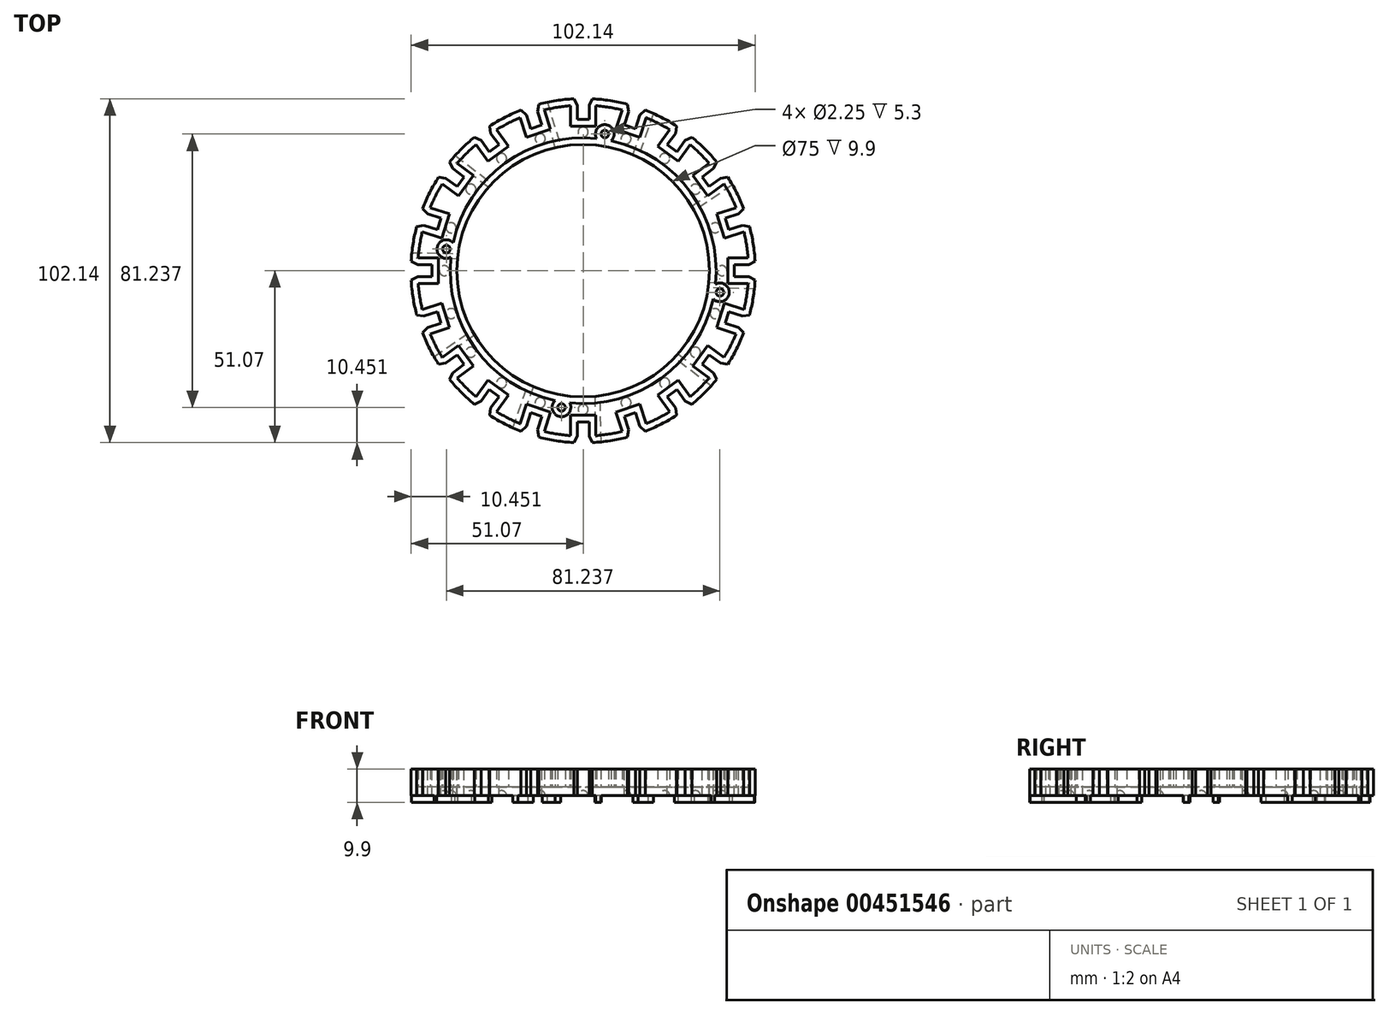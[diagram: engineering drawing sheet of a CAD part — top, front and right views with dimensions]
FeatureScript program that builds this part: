
annotation { "Feature Type Name" : "Feature", "Feature Type Description" : "" }
export const myFeature = defineFeature(function(context is Context, id is Id, definition is map)
    precondition{}
    {
        {
            var Q0;
            Q0=qCreatedBy(makeId("Top.planeOp"),FACE);
            var sketch = newSketch(context, id + "F0", { "sketchPlane" : qUnion([Q0])});
            skLineSegment(sketch, "E0.bottom", {"start": v(-1.78, -44.95) * mm, "end": v(1.77, -44.95) * mm});
            skLineSegment(sketch, "E0.left", {"start": v(-1.78, -44.95) * mm, "end": v(-1.78, -49.15) * mm});
            skLineSegment(sketch, "E0.right", {"start": v(1.77, -44.95) * mm, "end": v(1.77, -49.15) * mm});
            skLineSegment(sketch, "E1.0", {"start": v(-3.78, -42.95) * mm, "end": v(-3.78, -49) * mm});
            skLineSegment(sketch, "E1.1", {"start": v(-3.77, -42.95) * mm, "end": v(3.77, -42.95) * mm});
            skLineSegment(sketch, "E1.2", {"start": v(3.77, -42.95) * mm, "end": v(3.77, -49) * mm});
            skLineSegment(sketch, "E2", {"start": v(1.77, -49.15) * mm, "end": v(2.78, -51.07) * mm});
            skLineSegment(sketch, "E3", {"start": v(-1.78, -49.15) * mm, "end": v(-2.78, -51.07) * mm});
            skPoint(sketch, "E4.center", {"position": v(0, 0) * mm});
            skLineSegment(sketch, "E5.1.0", {"start": v(-16.86, -39.68) * mm, "end": v(-18.73, -45.44) * mm});
            skLineSegment(sketch, "E5.1.1", {"start": v(-9.68, -42.01) * mm, "end": v(-11.55, -47.77) * mm});
            skLineSegment(sketch, "E5.1.2", {"start": v(-16.86, -39.68) * mm, "end": v(-9.68, -42.01) * mm});
            skLineSegment(sketch, "E5.1.3", {"start": v(-12.2, -43.3) * mm, "end": v(-13.5, -47.3) * mm});
            skLineSegment(sketch, "E5.1.4", {"start": v(-16.88, -46.2) * mm, "end": v(-18.42, -47.72) * mm});
            skLineSegment(sketch, "E5.1.5", {"start": v(-15.58, -42.2) * mm, "end": v(-16.88, -46.2) * mm});
            skLineSegment(sketch, "E5.1.6", {"start": v(-13.5, -47.3) * mm, "end": v(-13.14, -49.43) * mm});
            skLineSegment(sketch, "E5.1.7", {"start": v(-15.58, -42.2) * mm, "end": v(-12.2, -43.3) * mm});
            skLineSegment(sketch, "E5.2.0", {"start": v(-28.3, -32.53) * mm, "end": v(-31.86, -37.43) * mm});
            skLineSegment(sketch, "E5.2.1", {"start": v(-22.2, -36.97) * mm, "end": v(-25.75, -41.86) * mm});
            skLineSegment(sketch, "E5.2.2", {"start": v(-28.3, -32.53) * mm, "end": v(-22.2, -36.97) * mm});
            skLineSegment(sketch, "E5.2.3", {"start": v(-24.98, -37.4) * mm, "end": v(-27.45, -40.8) * mm});
            skLineSegment(sketch, "E5.2.4", {"start": v(-30.33, -38.72) * mm, "end": v(-32.27, -39.69) * mm});
            skLineSegment(sketch, "E5.2.5", {"start": v(-27.86, -35.32) * mm, "end": v(-30.33, -38.72) * mm});
            skLineSegment(sketch, "E5.2.6", {"start": v(-27.45, -40.8) * mm, "end": v(-27.78, -42.95) * mm});
            skLineSegment(sketch, "E5.2.7", {"start": v(-27.86, -35.32) * mm, "end": v(-24.98, -37.4) * mm});
            skLineSegment(sketch, "E5.3.0", {"start": v(-36.97, -22.2) * mm, "end": v(-41.86, -25.75) * mm});
            skLineSegment(sketch, "E5.3.1", {"start": v(-32.53, -28.3) * mm, "end": v(-37.43, -31.86) * mm});
            skLineSegment(sketch, "E5.3.2", {"start": v(-36.97, -22.2) * mm, "end": v(-32.53, -28.3) * mm});
            skLineSegment(sketch, "E5.3.3", {"start": v(-35.32, -27.86) * mm, "end": v(-38.72, -30.33) * mm});
            skLineSegment(sketch, "E5.3.4", {"start": v(-40.8, -27.45) * mm, "end": v(-42.95, -27.78) * mm});
            skLineSegment(sketch, "E5.3.5", {"start": v(-37.4, -24.98) * mm, "end": v(-40.8, -27.45) * mm});
            skLineSegment(sketch, "E5.3.6", {"start": v(-38.72, -30.33) * mm, "end": v(-39.69, -32.27) * mm});
            skLineSegment(sketch, "E5.3.7", {"start": v(-37.4, -24.98) * mm, "end": v(-35.32, -27.86) * mm});
            skLineSegment(sketch, "E5.4.0", {"start": v(-42.01, -9.68) * mm, "end": v(-47.77, -11.55) * mm});
            skLineSegment(sketch, "E5.4.1", {"start": v(-39.68, -16.86) * mm, "end": v(-45.44, -18.73) * mm});
            skLineSegment(sketch, "E5.4.2", {"start": v(-42.01, -9.68) * mm, "end": v(-39.68, -16.86) * mm});
            skLineSegment(sketch, "E5.4.3", {"start": v(-42.2, -15.58) * mm, "end": v(-46.2, -16.88) * mm});
            skLineSegment(sketch, "E5.4.4", {"start": v(-47.3, -13.5) * mm, "end": v(-49.43, -13.14) * mm});
            skLineSegment(sketch, "E5.4.5", {"start": v(-43.3, -12.2) * mm, "end": v(-47.3, -13.5) * mm});
            skLineSegment(sketch, "E5.4.6", {"start": v(-46.2, -16.88) * mm, "end": v(-47.72, -18.42) * mm});
            skLineSegment(sketch, "E5.4.7", {"start": v(-43.3, -12.2) * mm, "end": v(-42.2, -15.58) * mm});
            skLineSegment(sketch, "E5.5.0", {"start": v(-42.95, 3.78) * mm, "end": v(-49, 3.78) * mm});
            skLineSegment(sketch, "E5.5.1", {"start": v(-42.95, -3.77) * mm, "end": v(-49, -3.77) * mm});
            skLineSegment(sketch, "E5.5.2", {"start": v(-42.95, 3.78) * mm, "end": v(-42.95, -3.77) * mm});
            skLineSegment(sketch, "E5.5.3", {"start": v(-44.95, -1.77) * mm, "end": v(-49.15, -1.77) * mm});
            skLineSegment(sketch, "E5.5.4", {"start": v(-49.15, 1.78) * mm, "end": v(-51.07, 2.78) * mm});
            skLineSegment(sketch, "E5.5.5", {"start": v(-44.95, 1.78) * mm, "end": v(-49.15, 1.78) * mm});
            skLineSegment(sketch, "E5.5.6", {"start": v(-49.15, -1.77) * mm, "end": v(-51.07, -2.78) * mm});
            skLineSegment(sketch, "E5.5.7", {"start": v(-44.95, 1.78) * mm, "end": v(-44.95, -1.77) * mm});
            skLineSegment(sketch, "E5.6.0", {"start": v(-39.68, 16.86) * mm, "end": v(-45.44, 18.73) * mm});
            skLineSegment(sketch, "E5.6.1", {"start": v(-42.01, 9.68) * mm, "end": v(-47.77, 11.55) * mm});
            skLineSegment(sketch, "E5.6.2", {"start": v(-39.68, 16.86) * mm, "end": v(-42.01, 9.68) * mm});
            skLineSegment(sketch, "E5.6.3", {"start": v(-43.3, 12.2) * mm, "end": v(-47.3, 13.5) * mm});
            skLineSegment(sketch, "E5.6.4", {"start": v(-46.2, 16.88) * mm, "end": v(-47.72, 18.42) * mm});
            skLineSegment(sketch, "E5.6.5", {"start": v(-42.2, 15.58) * mm, "end": v(-46.2, 16.88) * mm});
            skLineSegment(sketch, "E5.6.6", {"start": v(-47.3, 13.5) * mm, "end": v(-49.43, 13.14) * mm});
            skLineSegment(sketch, "E5.6.7", {"start": v(-42.2, 15.58) * mm, "end": v(-43.3, 12.2) * mm});
            skLineSegment(sketch, "E5.7.0", {"start": v(-32.53, 28.3) * mm, "end": v(-37.43, 31.86) * mm});
            skLineSegment(sketch, "E5.7.1", {"start": v(-36.97, 22.2) * mm, "end": v(-41.86, 25.75) * mm});
            skLineSegment(sketch, "E5.7.2", {"start": v(-32.53, 28.3) * mm, "end": v(-36.97, 22.2) * mm});
            skLineSegment(sketch, "E5.7.3", {"start": v(-37.4, 24.98) * mm, "end": v(-40.8, 27.45) * mm});
            skLineSegment(sketch, "E5.7.4", {"start": v(-38.72, 30.33) * mm, "end": v(-39.69, 32.27) * mm});
            skLineSegment(sketch, "E5.7.5", {"start": v(-35.32, 27.86) * mm, "end": v(-38.72, 30.33) * mm});
            skLineSegment(sketch, "E5.7.6", {"start": v(-40.8, 27.45) * mm, "end": v(-42.95, 27.78) * mm});
            skLineSegment(sketch, "E5.7.7", {"start": v(-35.32, 27.86) * mm, "end": v(-37.4, 24.98) * mm});
            skLineSegment(sketch, "E5.8.0", {"start": v(-22.2, 36.97) * mm, "end": v(-25.75, 41.86) * mm});
            skLineSegment(sketch, "E5.8.1", {"start": v(-28.3, 32.53) * mm, "end": v(-31.86, 37.43) * mm});
            skLineSegment(sketch, "E5.8.2", {"start": v(-22.2, 36.97) * mm, "end": v(-28.3, 32.53) * mm});
            skLineSegment(sketch, "E5.8.3", {"start": v(-27.86, 35.32) * mm, "end": v(-30.33, 38.72) * mm});
            skLineSegment(sketch, "E5.8.4", {"start": v(-27.45, 40.8) * mm, "end": v(-27.78, 42.95) * mm});
            skLineSegment(sketch, "E5.8.5", {"start": v(-24.98, 37.4) * mm, "end": v(-27.45, 40.8) * mm});
            skLineSegment(sketch, "E5.8.6", {"start": v(-30.33, 38.72) * mm, "end": v(-32.27, 39.69) * mm});
            skLineSegment(sketch, "E5.8.7", {"start": v(-24.98, 37.4) * mm, "end": v(-27.86, 35.32) * mm});
            skLineSegment(sketch, "E5.9.0", {"start": v(-9.68, 42.01) * mm, "end": v(-11.55, 47.77) * mm});
            skLineSegment(sketch, "E5.9.1", {"start": v(-16.86, 39.68) * mm, "end": v(-18.73, 45.44) * mm});
            skLineSegment(sketch, "E5.9.2", {"start": v(-9.68, 42.01) * mm, "end": v(-16.86, 39.68) * mm});
            skLineSegment(sketch, "E5.9.3", {"start": v(-15.58, 42.2) * mm, "end": v(-16.88, 46.2) * mm});
            skLineSegment(sketch, "E5.9.4", {"start": v(-13.5, 47.3) * mm, "end": v(-13.14, 49.43) * mm});
            skLineSegment(sketch, "E5.9.5", {"start": v(-12.2, 43.3) * mm, "end": v(-13.5, 47.3) * mm});
            skLineSegment(sketch, "E5.9.6", {"start": v(-16.88, 46.2) * mm, "end": v(-18.42, 47.72) * mm});
            skLineSegment(sketch, "E5.9.7", {"start": v(-12.2, 43.3) * mm, "end": v(-15.58, 42.2) * mm});
            skLineSegment(sketch, "E5.10.0", {"start": v(3.78, 42.95) * mm, "end": v(3.78, 49) * mm});
            skLineSegment(sketch, "E5.10.1", {"start": v(-3.77, 42.95) * mm, "end": v(-3.77, 49) * mm});
            skLineSegment(sketch, "E5.10.2", {"start": v(3.78, 42.95) * mm, "end": v(-3.77, 42.95) * mm});
            skLineSegment(sketch, "E5.10.3", {"start": v(-1.77, 44.95) * mm, "end": v(-1.77, 49.15) * mm});
            skLineSegment(sketch, "E5.10.4", {"start": v(1.78, 49.15) * mm, "end": v(2.78, 51.07) * mm});
            skLineSegment(sketch, "E5.10.5", {"start": v(1.78, 44.95) * mm, "end": v(1.78, 49.15) * mm});
            skLineSegment(sketch, "E5.10.6", {"start": v(-1.77, 49.15) * mm, "end": v(-2.78, 51.07) * mm});
            skLineSegment(sketch, "E5.10.7", {"start": v(1.78, 44.95) * mm, "end": v(-1.77, 44.95) * mm});
            skLineSegment(sketch, "E5.11.0", {"start": v(16.86, 39.68) * mm, "end": v(18.73, 45.44) * mm});
            skLineSegment(sketch, "E5.11.1", {"start": v(9.68, 42.01) * mm, "end": v(11.55, 47.77) * mm});
            skLineSegment(sketch, "E5.11.2", {"start": v(16.86, 39.68) * mm, "end": v(9.68, 42.01) * mm});
            skLineSegment(sketch, "E5.11.3", {"start": v(12.2, 43.3) * mm, "end": v(13.5, 47.3) * mm});
            skLineSegment(sketch, "E5.11.4", {"start": v(16.88, 46.2) * mm, "end": v(18.42, 47.72) * mm});
            skLineSegment(sketch, "E5.11.5", {"start": v(15.58, 42.2) * mm, "end": v(16.88, 46.2) * mm});
            skLineSegment(sketch, "E5.11.6", {"start": v(13.5, 47.3) * mm, "end": v(13.14, 49.43) * mm});
            skLineSegment(sketch, "E5.11.7", {"start": v(15.58, 42.2) * mm, "end": v(12.2, 43.3) * mm});
            skLineSegment(sketch, "E5.12.0", {"start": v(28.3, 32.53) * mm, "end": v(31.86, 37.43) * mm});
            skLineSegment(sketch, "E5.12.1", {"start": v(22.2, 36.97) * mm, "end": v(25.75, 41.86) * mm});
            skLineSegment(sketch, "E5.12.2", {"start": v(28.3, 32.53) * mm, "end": v(22.2, 36.97) * mm});
            skLineSegment(sketch, "E5.12.3", {"start": v(24.98, 37.4) * mm, "end": v(27.45, 40.8) * mm});
            skLineSegment(sketch, "E5.12.4", {"start": v(30.33, 38.72) * mm, "end": v(32.27, 39.69) * mm});
            skLineSegment(sketch, "E5.12.5", {"start": v(27.86, 35.32) * mm, "end": v(30.33, 38.72) * mm});
            skLineSegment(sketch, "E5.12.6", {"start": v(27.45, 40.8) * mm, "end": v(27.78, 42.95) * mm});
            skLineSegment(sketch, "E5.12.7", {"start": v(27.86, 35.32) * mm, "end": v(24.98, 37.4) * mm});
            skLineSegment(sketch, "E5.13.0", {"start": v(36.97, 22.2) * mm, "end": v(41.86, 25.75) * mm});
            skLineSegment(sketch, "E5.13.1", {"start": v(32.53, 28.3) * mm, "end": v(37.43, 31.86) * mm});
            skLineSegment(sketch, "E5.13.2", {"start": v(36.97, 22.2) * mm, "end": v(32.53, 28.3) * mm});
            skLineSegment(sketch, "E5.13.3", {"start": v(35.32, 27.86) * mm, "end": v(38.72, 30.33) * mm});
            skLineSegment(sketch, "E5.13.4", {"start": v(40.8, 27.45) * mm, "end": v(42.95, 27.78) * mm});
            skLineSegment(sketch, "E5.13.5", {"start": v(37.4, 24.98) * mm, "end": v(40.8, 27.45) * mm});
            skLineSegment(sketch, "E5.13.6", {"start": v(38.72, 30.33) * mm, "end": v(39.69, 32.27) * mm});
            skLineSegment(sketch, "E5.13.7", {"start": v(37.4, 24.98) * mm, "end": v(35.32, 27.86) * mm});
            skLineSegment(sketch, "E5.14.0", {"start": v(42.01, 9.68) * mm, "end": v(47.77, 11.55) * mm});
            skLineSegment(sketch, "E5.14.1", {"start": v(39.68, 16.86) * mm, "end": v(45.44, 18.73) * mm});
            skLineSegment(sketch, "E5.14.2", {"start": v(42.01, 9.68) * mm, "end": v(39.68, 16.86) * mm});
            skLineSegment(sketch, "E5.14.3", {"start": v(42.2, 15.58) * mm, "end": v(46.2, 16.88) * mm});
            skLineSegment(sketch, "E5.14.4", {"start": v(47.3, 13.5) * mm, "end": v(49.43, 13.14) * mm});
            skLineSegment(sketch, "E5.14.5", {"start": v(43.3, 12.2) * mm, "end": v(47.3, 13.5) * mm});
            skLineSegment(sketch, "E5.14.6", {"start": v(46.2, 16.88) * mm, "end": v(47.72, 18.42) * mm});
            skLineSegment(sketch, "E5.14.7", {"start": v(43.3, 12.2) * mm, "end": v(42.2, 15.58) * mm});
            skLineSegment(sketch, "E5.15.0", {"start": v(42.95, -3.78) * mm, "end": v(49, -3.78) * mm});
            skLineSegment(sketch, "E5.15.1", {"start": v(42.95, 3.77) * mm, "end": v(49, 3.77) * mm});
            skLineSegment(sketch, "E5.15.2", {"start": v(42.95, -3.78) * mm, "end": v(42.95, 3.77) * mm});
            skLineSegment(sketch, "E5.15.3", {"start": v(44.95, 1.77) * mm, "end": v(49.15, 1.77) * mm});
            skLineSegment(sketch, "E5.15.4", {"start": v(49.15, -1.78) * mm, "end": v(51.07, -2.78) * mm});
            skLineSegment(sketch, "E5.15.5", {"start": v(44.95, -1.78) * mm, "end": v(49.15, -1.78) * mm});
            skLineSegment(sketch, "E5.15.6", {"start": v(49.15, 1.77) * mm, "end": v(51.07, 2.78) * mm});
            skLineSegment(sketch, "E5.15.7", {"start": v(44.95, -1.78) * mm, "end": v(44.95, 1.77) * mm});
            skLineSegment(sketch, "E5.16.0", {"start": v(39.68, -16.86) * mm, "end": v(45.44, -18.73) * mm});
            skLineSegment(sketch, "E5.16.1", {"start": v(42.01, -9.68) * mm, "end": v(47.77, -11.55) * mm});
            skLineSegment(sketch, "E5.16.2", {"start": v(39.68, -16.86) * mm, "end": v(42.01, -9.68) * mm});
            skLineSegment(sketch, "E5.16.3", {"start": v(43.3, -12.2) * mm, "end": v(47.3, -13.5) * mm});
            skLineSegment(sketch, "E5.16.4", {"start": v(46.2, -16.88) * mm, "end": v(47.72, -18.42) * mm});
            skLineSegment(sketch, "E5.16.5", {"start": v(42.2, -15.58) * mm, "end": v(46.2, -16.88) * mm});
            skLineSegment(sketch, "E5.16.6", {"start": v(47.3, -13.5) * mm, "end": v(49.43, -13.14) * mm});
            skLineSegment(sketch, "E5.16.7", {"start": v(42.2, -15.58) * mm, "end": v(43.3, -12.2) * mm});
            skLineSegment(sketch, "E5.17.0", {"start": v(32.53, -28.3) * mm, "end": v(37.43, -31.86) * mm});
            skLineSegment(sketch, "E5.17.1", {"start": v(36.97, -22.2) * mm, "end": v(41.86, -25.75) * mm});
            skLineSegment(sketch, "E5.17.2", {"start": v(32.53, -28.3) * mm, "end": v(36.97, -22.2) * mm});
            skLineSegment(sketch, "E5.17.3", {"start": v(37.4, -24.98) * mm, "end": v(40.8, -27.45) * mm});
            skLineSegment(sketch, "E5.17.4", {"start": v(38.72, -30.33) * mm, "end": v(39.69, -32.27) * mm});
            skLineSegment(sketch, "E5.17.5", {"start": v(35.32, -27.86) * mm, "end": v(38.72, -30.33) * mm});
            skLineSegment(sketch, "E5.17.6", {"start": v(40.8, -27.45) * mm, "end": v(42.95, -27.78) * mm});
            skLineSegment(sketch, "E5.17.7", {"start": v(35.32, -27.86) * mm, "end": v(37.4, -24.98) * mm});
            skLineSegment(sketch, "E5.18.0", {"start": v(22.2, -36.97) * mm, "end": v(25.75, -41.86) * mm});
            skLineSegment(sketch, "E5.18.1", {"start": v(28.3, -32.53) * mm, "end": v(31.86, -37.43) * mm});
            skLineSegment(sketch, "E5.18.2", {"start": v(22.2, -36.97) * mm, "end": v(28.3, -32.53) * mm});
            skLineSegment(sketch, "E5.18.3", {"start": v(27.86, -35.32) * mm, "end": v(30.33, -38.72) * mm});
            skLineSegment(sketch, "E5.18.4", {"start": v(27.45, -40.8) * mm, "end": v(27.78, -42.95) * mm});
            skLineSegment(sketch, "E5.18.5", {"start": v(24.98, -37.4) * mm, "end": v(27.45, -40.8) * mm});
            skLineSegment(sketch, "E5.18.6", {"start": v(30.33, -38.72) * mm, "end": v(32.27, -39.69) * mm});
            skLineSegment(sketch, "E5.18.7", {"start": v(24.98, -37.4) * mm, "end": v(27.86, -35.32) * mm});
            skLineSegment(sketch, "E5.19.0", {"start": v(9.68, -42.01) * mm, "end": v(11.55, -47.77) * mm});
            skLineSegment(sketch, "E5.19.1", {"start": v(16.86, -39.68) * mm, "end": v(18.73, -45.44) * mm});
            skLineSegment(sketch, "E5.19.2", {"start": v(9.68, -42.01) * mm, "end": v(16.86, -39.68) * mm});
            skLineSegment(sketch, "E5.19.3", {"start": v(15.58, -42.2) * mm, "end": v(16.88, -46.2) * mm});
            skLineSegment(sketch, "E5.19.4", {"start": v(13.5, -47.3) * mm, "end": v(13.14, -49.43) * mm});
            skLineSegment(sketch, "E5.19.5", {"start": v(12.2, -43.3) * mm, "end": v(13.5, -47.3) * mm});
            skLineSegment(sketch, "E5.19.6", {"start": v(16.88, -46.2) * mm, "end": v(18.42, -47.72) * mm});
            skLineSegment(sketch, "E5.19.7", {"start": v(12.2, -43.3) * mm, "end": v(15.58, -42.2) * mm});
            skLineSegment(sketch, "E5.anchor1", {"start": v(0, 0) * mm, "end": v(-2.78, -51.07) * mm, "construction": true});
            skLineSegment(sketch, "E5.anchor2", {"start": v(0, 0) * mm, "end": v(13.14, -49.43) * mm, "construction": true});
            skArc(sketch, "E6", {"start": v(-3.78, -49) * mm, "mid": v(-7.69, -48.54) * mm, "end": v(-11.55, -47.77) * mm});
            skArc(sketch, "E7", {"start": v(-2.78, -51.07) * mm, "mid": v(-8, -50.52) * mm, "end": v(-13.14, -49.43) * mm});
            skArc(sketch, "E8.1.0", {"start": v(-18.73, -45.44) * mm, "mid": v(-22.31, -43.8) * mm, "end": v(-25.75, -41.86) * mm});
            skArc(sketch, "E8.1.1", {"start": v(-18.42, -47.72) * mm, "mid": v(-23.22, -45.57) * mm, "end": v(-27.78, -42.95) * mm});
            skArc(sketch, "E8.2.0", {"start": v(-31.86, -37.43) * mm, "mid": v(-34.75, -34.75) * mm, "end": v(-37.43, -31.86) * mm});
            skArc(sketch, "E8.2.1", {"start": v(-32.27, -39.69) * mm, "mid": v(-36.17, -36.17) * mm, "end": v(-39.69, -32.27) * mm});
            skArc(sketch, "E8.3.0", {"start": v(-41.86, -25.75) * mm, "mid": v(-43.8, -22.31) * mm, "end": v(-45.44, -18.73) * mm});
            skArc(sketch, "E8.3.1", {"start": v(-42.95, -27.78) * mm, "mid": v(-45.57, -23.22) * mm, "end": v(-47.72, -18.42) * mm});
            skArc(sketch, "E8.4.0", {"start": v(-47.77, -11.55) * mm, "mid": v(-48.54, -7.69) * mm, "end": v(-49, -3.77) * mm});
            skArc(sketch, "E8.4.1", {"start": v(-49.43, -13.14) * mm, "mid": v(-50.52, -8) * mm, "end": v(-51.07, -2.78) * mm});
            skArc(sketch, "E8.5.0", {"start": v(-49, 3.78) * mm, "mid": v(-48.54, 7.69) * mm, "end": v(-47.77, 11.55) * mm});
            skArc(sketch, "E8.5.1", {"start": v(-51.07, 2.78) * mm, "mid": v(-50.52, 8) * mm, "end": v(-49.43, 13.14) * mm});
            skArc(sketch, "E8.6.0", {"start": v(-45.44, 18.73) * mm, "mid": v(-43.8, 22.31) * mm, "end": v(-41.86, 25.75) * mm});
            skArc(sketch, "E8.6.1", {"start": v(-47.72, 18.42) * mm, "mid": v(-45.57, 23.22) * mm, "end": v(-42.95, 27.78) * mm});
            skArc(sketch, "E8.7.0", {"start": v(-37.43, 31.86) * mm, "mid": v(-34.75, 34.75) * mm, "end": v(-31.86, 37.43) * mm});
            skArc(sketch, "E8.7.1", {"start": v(-39.69, 32.27) * mm, "mid": v(-36.17, 36.17) * mm, "end": v(-32.27, 39.69) * mm});
            skArc(sketch, "E8.8.0", {"start": v(-25.75, 41.86) * mm, "mid": v(-22.31, 43.8) * mm, "end": v(-18.73, 45.44) * mm});
            skArc(sketch, "E8.8.1", {"start": v(-27.78, 42.95) * mm, "mid": v(-23.22, 45.57) * mm, "end": v(-18.42, 47.72) * mm});
            skArc(sketch, "E8.9.0", {"start": v(-11.55, 47.77) * mm, "mid": v(-7.69, 48.54) * mm, "end": v(-3.77, 49) * mm});
            skArc(sketch, "E8.9.1", {"start": v(-13.14, 49.43) * mm, "mid": v(-8, 50.52) * mm, "end": v(-2.78, 51.07) * mm});
            skArc(sketch, "E8.10.0", {"start": v(3.78, 49) * mm, "mid": v(7.69, 48.54) * mm, "end": v(11.55, 47.77) * mm});
            skArc(sketch, "E8.10.1", {"start": v(2.78, 51.07) * mm, "mid": v(8, 50.52) * mm, "end": v(13.14, 49.43) * mm});
            skArc(sketch, "E8.11.0", {"start": v(18.73, 45.44) * mm, "mid": v(22.31, 43.8) * mm, "end": v(25.75, 41.86) * mm});
            skArc(sketch, "E8.11.1", {"start": v(18.42, 47.72) * mm, "mid": v(23.22, 45.57) * mm, "end": v(27.78, 42.95) * mm});
            skArc(sketch, "E8.12.0", {"start": v(31.86, 37.43) * mm, "mid": v(34.75, 34.75) * mm, "end": v(37.43, 31.86) * mm});
            skArc(sketch, "E8.12.1", {"start": v(32.27, 39.69) * mm, "mid": v(36.17, 36.17) * mm, "end": v(39.69, 32.27) * mm});
            skArc(sketch, "E8.13.0", {"start": v(41.86, 25.75) * mm, "mid": v(43.8, 22.31) * mm, "end": v(45.44, 18.73) * mm});
            skArc(sketch, "E8.13.1", {"start": v(42.95, 27.78) * mm, "mid": v(45.57, 23.22) * mm, "end": v(47.72, 18.42) * mm});
            skArc(sketch, "E8.14.0", {"start": v(47.77, 11.55) * mm, "mid": v(48.54, 7.69) * mm, "end": v(49, 3.77) * mm});
            skArc(sketch, "E8.14.1", {"start": v(49.43, 13.14) * mm, "mid": v(50.52, 8) * mm, "end": v(51.07, 2.78) * mm});
            skArc(sketch, "E8.15.0", {"start": v(49, -3.78) * mm, "mid": v(48.54, -7.69) * mm, "end": v(47.77, -11.55) * mm});
            skArc(sketch, "E8.15.1", {"start": v(51.07, -2.78) * mm, "mid": v(50.52, -8) * mm, "end": v(49.43, -13.14) * mm});
            skArc(sketch, "E8.16.0", {"start": v(45.44, -18.73) * mm, "mid": v(43.8, -22.31) * mm, "end": v(41.86, -25.75) * mm});
            skArc(sketch, "E8.16.1", {"start": v(47.72, -18.42) * mm, "mid": v(45.57, -23.22) * mm, "end": v(42.95, -27.78) * mm});
            skArc(sketch, "E8.17.0", {"start": v(37.43, -31.86) * mm, "mid": v(34.75, -34.75) * mm, "end": v(31.86, -37.43) * mm});
            skArc(sketch, "E8.17.1", {"start": v(39.69, -32.27) * mm, "mid": v(36.17, -36.17) * mm, "end": v(32.27, -39.69) * mm});
            skArc(sketch, "E8.18.0", {"start": v(25.75, -41.86) * mm, "mid": v(22.31, -43.8) * mm, "end": v(18.73, -45.44) * mm});
            skArc(sketch, "E8.18.1", {"start": v(27.78, -42.95) * mm, "mid": v(23.22, -45.57) * mm, "end": v(18.42, -47.72) * mm});
            skArc(sketch, "E8.19.0", {"start": v(11.55, -47.77) * mm, "mid": v(7.69, -48.54) * mm, "end": v(3.77, -49) * mm});
            skArc(sketch, "E8.19.1", {"start": v(13.14, -49.43) * mm, "mid": v(8, -50.52) * mm, "end": v(2.78, -51.07) * mm});
            skLineSegment(sketch, "E8.anchor1", {"start": v(0, 0) * mm, "end": v(-13.14, -49.43) * mm, "construction": true});
            skLineSegment(sketch, "E8.anchor2", {"start": v(0, 0) * mm, "end": v(2.78, -51.07) * mm, "construction": true});
            skLineSegment(sketch, "E9", {"start": v(0, 0) * mm, "end": v(-7.69, -48.54) * mm, "construction": true});
            skCircle(sketch, "E10", {"center": v(0, 0) * mm, "radius": 37.5 * mm});
            skArc(sketch, "E11.0", {"start": v(39.3, -4) * mm, "mid": v(31.96, 23.22) * mm, "end": v(8.35, 38.6) * mm});
            skCircle(sketch, "E12", {"center": v(-6.43, -40.62) * mm, "radius": 2.77 * mm});
            skCircle(sketch, "E13.0", {"center": v(-6.43, -40.62) * mm, "radius": 1.13 * mm});
            skCircle(sketch, "E14.1.0", {"center": v(-40.62, 6.43) * mm, "radius": 2.77 * mm});
            skCircle(sketch, "E14.1.1", {"center": v(-40.62, 6.43) * mm, "radius": 1.13 * mm});
            skCircle(sketch, "E14.2.0", {"center": v(6.43, 40.62) * mm, "radius": 2.77 * mm});
            skCircle(sketch, "E14.2.1", {"center": v(6.43, 40.62) * mm, "radius": 1.13 * mm});
            skCircle(sketch, "E14.3.0", {"center": v(40.62, -6.43) * mm, "radius": 2.77 * mm});
            skCircle(sketch, "E14.3.1", {"center": v(40.62, -6.43) * mm, "radius": 1.13 * mm});
            skLineSegment(sketch, "E14.anchor1", {"start": v(0, 0) * mm, "end": v(-6.43, -40.62) * mm, "construction": true});
            skLineSegment(sketch, "E14.anchor2", {"start": v(0, 0) * mm, "end": v(40.62, -6.43) * mm, "construction": true});
            skArc(sketch, "E15.trimOffspring", {"start": v(4, 39.3) * mm, "mid": v(-23.22, 31.96) * mm, "end": v(-38.6, 8.35) * mm});
            skArc(sketch, "E16.trimOffspring", {"start": v(-39.3, 4) * mm, "mid": v(-31.96, -23.22) * mm, "end": v(-8.35, -38.6) * mm});
            skArc(sketch, "E17.trimOffspring", {"start": v(-4, -39.3) * mm, "mid": v(23.22, -31.96) * mm, "end": v(38.6, -8.35) * mm});
            skSolve(sketch);
        }
        {
            var Q0;
            Q0=makeQuery(id+"F0.imprint","IMPRINT",FACE,{"disambiguationData":[TD([[makeQuery(id+"F0.imprint","IMPRINT",EDGE,{"derivedFrom":sQuery(id+"F0.wireOp",EDGE,"E1.0")}),-1.0]])]});
            var Q1;
            Q1=makeQuery(id+"F0.imprint","IMPRINT",FACE,{"disambiguationData":[TD([[makeQuery(id+"F0.imprint","IMPRINT",EDGE,{"derivedFrom":sQuery(id+"F0.wireOp",EDGE,"E0.bottom")}),1.0]])]});
            var Q2;
            Q2=makeQuery(id+"F0.imprint","IMPRINT",FACE,{"disambiguationData":[TD([[makeQuery(id+"F0.imprint","IMPRINT",EDGE,{"derivedFrom":sQuery(id+"F0.wireOp",EDGE,"E10")}),-1.0]])]});
            var Q3;
            Q3=makeQuery(id+"F0.imprint","IMPRINT",FACE,{"disambiguationData":[TD([[makeQuery(id+"F0.imprint","IMPRINT",EDGE,{"derivedFrom":sQuery(id+"F0.wireOp",EDGE,"E14.2.1")}),-1.0]])]});
            var Q4;
            Q4=makeQuery(id+"F0.imprint","IMPRINT",FACE,{"disambiguationData":[TD([[makeQuery(id+"F0.imprint","IMPRINT",EDGE,{"derivedFrom":sQuery(id+"F0.wireOp",EDGE,"E14.2.1")}),1.0]])]});
            var Q5;
            Q5=makeQuery(id+"F0.imprint","IMPRINT",FACE,{"disambiguationData":[TD([[makeQuery(id+"F0.imprint","IMPRINT",EDGE,{"derivedFrom":sQuery(id+"F0.wireOp",EDGE,"E14.1.1")}),-1.0]])]});
            var Q6;
            Q6=makeQuery(id+"F0.imprint","IMPRINT",FACE,{"disambiguationData":[TD([[makeQuery(id+"F0.imprint","IMPRINT",EDGE,{"derivedFrom":sQuery(id+"F0.wireOp",EDGE,"E14.1.1")}),1.0]])]});
            var Q7;
            Q7=makeQuery(id+"F0.imprint","IMPRINT",FACE,{"disambiguationData":[TD([[makeQuery(id+"F0.imprint","IMPRINT",EDGE,{"derivedFrom":sQuery(id+"F0.wireOp",EDGE,"E13.0")}),-1.0]])]});
            var Q8;
            Q8=makeQuery(id+"F0.imprint","IMPRINT",FACE,{"disambiguationData":[TD([[makeQuery(id+"F0.imprint","IMPRINT",EDGE,{"derivedFrom":sQuery(id+"F0.wireOp",EDGE,"E13.0")}),1.0]])]});
            var Q9;
            Q9=makeQuery(id+"F0.imprint","IMPRINT",FACE,{"disambiguationData":[TD([[makeQuery(id+"F0.imprint","IMPRINT",EDGE,{"derivedFrom":sQuery(id+"F0.wireOp",EDGE,"E14.3.1")}),-1.0]])]});
            var Q10;
            Q10=makeQuery(id+"F0.imprint","IMPRINT",FACE,{"disambiguationData":[TD([[makeQuery(id+"F0.imprint","IMPRINT",EDGE,{"derivedFrom":sQuery(id+"F0.wireOp",EDGE,"E14.3.1")}),1.0]])]});
            extrude(context, id + "F1", {"entities" : qUnion([Q0, Q1, Q2, Q3, Q4, Q5, Q6, Q7, Q8, Q9, Q10]), "oppositeDirection" : true, "depth" : 2.6 * mm, "offsetDistance" : 25 * mm});
        }
        {
            var Q0;
            Q0=makeQuery(id+"F0.imprint","IMPRINT",FACE,{"disambiguationData":[TD([[makeQuery(id+"F0.imprint","IMPRINT",EDGE,{"derivedFrom":sQuery(id+"F0.wireOp",EDGE,"E0.bottom")}),1.0]])]});
            var Q1;
            Q1=makeQuery(id+"F0.imprint","IMPRINT",FACE,{"disambiguationData":[TD([[makeQuery(id+"F0.imprint","IMPRINT",EDGE,{"derivedFrom":sQuery(id+"F0.wireOp",EDGE,"E10")}),-1.0]])]});
            var Q2;
            Q2=makeQuery(id+"F0.imprint","IMPRINT",FACE,{"disambiguationData":[TD([[makeQuery(id+"F0.imprint","IMPRINT",EDGE,{"derivedFrom":sQuery(id+"F0.wireOp",EDGE,"E14.2.1")}),-1.0]])]});
            var Q3;
            Q3=makeQuery(id+"F0.imprint","IMPRINT",FACE,{"disambiguationData":[TD([[makeQuery(id+"F0.imprint","IMPRINT",EDGE,{"derivedFrom":sQuery(id+"F0.wireOp",EDGE,"E14.3.1")}),-1.0]])]});
            var Q4;
            Q4=makeQuery(id+"F0.imprint","IMPRINT",FACE,{"disambiguationData":[TD([[makeQuery(id+"F0.imprint","IMPRINT",EDGE,{"derivedFrom":sQuery(id+"F0.wireOp",EDGE,"E13.0")}),-1.0]])]});
            var Q5;
            Q5=makeQuery(id+"F0.imprint","IMPRINT",FACE,{"disambiguationData":[TD([[makeQuery(id+"F0.imprint","IMPRINT",EDGE,{"derivedFrom":sQuery(id+"F0.wireOp",EDGE,"E14.1.1")}),-1.0]])]});
            extrude(context, id + "F2", {"entities" : qUnion([Q0, Q1, Q2, Q3, Q4, Q5]), "operationType" : NewBodyOperationType.ADD, "depth" : 5.3 * mm, "offsetDistance" : 25 * mm});
        }
        {
            var Q0;
            Q0=makeQuery(id+"F1.opExtrude","CAP_FACE",FACE,{"disambiguationData":[OSD([sQuery(id+"F0.wireOp",EDGE,"E0.bottom"),sQuery(id+"F0.wireOp",EDGE,"E0.left"),sQuery(id+"F0.wireOp",EDGE,"E0.right"),sQuery(id+"F0.wireOp",EDGE,"E2"),sQuery(id+"F0.wireOp",EDGE,"E3"),sQuery(id+"F0.wireOp",EDGE,"E5.1.3"),sQuery(id+"F0.wireOp",EDGE,"E5.1.4"),sQuery(id+"F0.wireOp",EDGE,"E5.1.5"),sQuery(id+"F0.wireOp",EDGE,"E5.1.6"),sQuery(id+"F0.wireOp",EDGE,"E5.1.7"),sQuery(id+"F0.wireOp",EDGE,"E5.2.3"),sQuery(id+"F0.wireOp",EDGE,"E5.2.4"),sQuery(id+"F0.wireOp",EDGE,"E5.2.5"),sQuery(id+"F0.wireOp",EDGE,"E5.2.6"),sQuery(id+"F0.wireOp",EDGE,"E5.2.7"),sQuery(id+"F0.wireOp",EDGE,"E5.3.3"),sQuery(id+"F0.wireOp",EDGE,"E5.3.4"),sQuery(id+"F0.wireOp",EDGE,"E5.3.5"),sQuery(id+"F0.wireOp",EDGE,"E5.3.6"),sQuery(id+"F0.wireOp",EDGE,"E5.3.7"),sQuery(id+"F0.wireOp",EDGE,"E5.4.3"),sQuery(id+"F0.wireOp",EDGE,"E5.4.4"),sQuery(id+"F0.wireOp",EDGE,"E5.4.5"),sQuery(id+"F0.wireOp",EDGE,"E5.4.6"),sQuery(id+"F0.wireOp",EDGE,"E5.4.7"),sQuery(id+"F0.wireOp",EDGE,"E5.5.3"),sQuery(id+"F0.wireOp",EDGE,"E5.5.4"),sQuery(id+"F0.wireOp",EDGE,"E5.5.5"),sQuery(id+"F0.wireOp",EDGE,"E5.5.6"),sQuery(id+"F0.wireOp",EDGE,"E5.5.7"),sQuery(id+"F0.wireOp",EDGE,"E5.6.3"),sQuery(id+"F0.wireOp",EDGE,"E5.6.4"),sQuery(id+"F0.wireOp",EDGE,"E5.6.5"),sQuery(id+"F0.wireOp",EDGE,"E5.6.6"),sQuery(id+"F0.wireOp",EDGE,"E5.6.7"),sQuery(id+"F0.wireOp",EDGE,"E5.7.3"),sQuery(id+"F0.wireOp",EDGE,"E5.7.4"),sQuery(id+"F0.wireOp",EDGE,"E5.7.5"),sQuery(id+"F0.wireOp",EDGE,"E5.7.6"),sQuery(id+"F0.wireOp",EDGE,"E5.7.7"),sQuery(id+"F0.wireOp",EDGE,"E5.8.3"),sQuery(id+"F0.wireOp",EDGE,"E5.8.4"),sQuery(id+"F0.wireOp",EDGE,"E5.8.5"),sQuery(id+"F0.wireOp",EDGE,"E5.8.6"),sQuery(id+"F0.wireOp",EDGE,"E5.8.7"),sQuery(id+"F0.wireOp",EDGE,"E5.9.3"),sQuery(id+"F0.wireOp",EDGE,"E5.9.4"),sQuery(id+"F0.wireOp",EDGE,"E5.9.5"),sQuery(id+"F0.wireOp",EDGE,"E5.9.6"),sQuery(id+"F0.wireOp",EDGE,"E5.9.7"),sQuery(id+"F0.wireOp",EDGE,"E5.10.3"),sQuery(id+"F0.wireOp",EDGE,"E5.10.4"),sQuery(id+"F0.wireOp",EDGE,"E5.10.5"),sQuery(id+"F0.wireOp",EDGE,"E5.10.6"),sQuery(id+"F0.wireOp",EDGE,"E5.10.7"),sQuery(id+"F0.wireOp",EDGE,"E5.11.3"),sQuery(id+"F0.wireOp",EDGE,"E5.11.4"),sQuery(id+"F0.wireOp",EDGE,"E5.11.5"),sQuery(id+"F0.wireOp",EDGE,"E5.11.6"),sQuery(id+"F0.wireOp",EDGE,"E5.11.7"),sQuery(id+"F0.wireOp",EDGE,"E5.12.3"),sQuery(id+"F0.wireOp",EDGE,"E5.12.4"),sQuery(id+"F0.wireOp",EDGE,"E5.12.5"),sQuery(id+"F0.wireOp",EDGE,"E5.12.6"),sQuery(id+"F0.wireOp",EDGE,"E5.12.7"),sQuery(id+"F0.wireOp",EDGE,"E5.13.3"),sQuery(id+"F0.wireOp",EDGE,"E5.13.4"),sQuery(id+"F0.wireOp",EDGE,"E5.13.5"),sQuery(id+"F0.wireOp",EDGE,"E5.13.6"),sQuery(id+"F0.wireOp",EDGE,"E5.13.7"),sQuery(id+"F0.wireOp",EDGE,"E5.14.3"),sQuery(id+"F0.wireOp",EDGE,"E5.14.4"),sQuery(id+"F0.wireOp",EDGE,"E5.14.5"),sQuery(id+"F0.wireOp",EDGE,"E5.14.6"),sQuery(id+"F0.wireOp",EDGE,"E5.14.7"),sQuery(id+"F0.wireOp",EDGE,"E5.15.3"),sQuery(id+"F0.wireOp",EDGE,"E5.15.4"),sQuery(id+"F0.wireOp",EDGE,"E5.15.5"),sQuery(id+"F0.wireOp",EDGE,"E5.15.6"),sQuery(id+"F0.wireOp",EDGE,"E5.15.7"),sQuery(id+"F0.wireOp",EDGE,"E5.16.3"),sQuery(id+"F0.wireOp",EDGE,"E5.16.4"),sQuery(id+"F0.wireOp",EDGE,"E5.16.5"),sQuery(id+"F0.wireOp",EDGE,"E5.16.6"),sQuery(id+"F0.wireOp",EDGE,"E5.16.7"),sQuery(id+"F0.wireOp",EDGE,"E5.17.3"),sQuery(id+"F0.wireOp",EDGE,"E5.17.4"),sQuery(id+"F0.wireOp",EDGE,"E5.17.5"),sQuery(id+"F0.wireOp",EDGE,"E5.17.6"),sQuery(id+"F0.wireOp",EDGE,"E5.17.7"),sQuery(id+"F0.wireOp",EDGE,"E5.18.3"),sQuery(id+"F0.wireOp",EDGE,"E5.18.4"),sQuery(id+"F0.wireOp",EDGE,"E5.18.5"),sQuery(id+"F0.wireOp",EDGE,"E5.18.6"),sQuery(id+"F0.wireOp",EDGE,"E5.18.7"),sQuery(id+"F0.wireOp",EDGE,"E5.19.3"),sQuery(id+"F0.wireOp",EDGE,"E5.19.4"),sQuery(id+"F0.wireOp",EDGE,"E5.19.5"),sQuery(id+"F0.wireOp",EDGE,"E5.19.6"),sQuery(id+"F0.wireOp",EDGE,"E5.19.7"),sQuery(id+"F0.wireOp",EDGE,"E7"),sQuery(id+"F0.wireOp",EDGE,"E8.1.1"),sQuery(id+"F0.wireOp",EDGE,"E8.2.1"),sQuery(id+"F0.wireOp",EDGE,"E8.3.1"),sQuery(id+"F0.wireOp",EDGE,"E8.4.1"),sQuery(id+"F0.wireOp",EDGE,"E8.5.1"),sQuery(id+"F0.wireOp",EDGE,"E8.6.1"),sQuery(id+"F0.wireOp",EDGE,"E8.7.1"),sQuery(id+"F0.wireOp",EDGE,"E8.8.1"),sQuery(id+"F0.wireOp",EDGE,"E8.9.1"),sQuery(id+"F0.wireOp",EDGE,"E8.10.1"),sQuery(id+"F0.wireOp",EDGE,"E8.11.1"),sQuery(id+"F0.wireOp",EDGE,"E8.12.1"),sQuery(id+"F0.wireOp",EDGE,"E8.13.1"),sQuery(id+"F0.wireOp",EDGE,"E8.14.1"),sQuery(id+"F0.wireOp",EDGE,"E8.15.1"),sQuery(id+"F0.wireOp",EDGE,"E8.16.1"),sQuery(id+"F0.wireOp",EDGE,"E8.17.1"),sQuery(id+"F0.wireOp",EDGE,"E8.18.1"),sQuery(id+"F0.wireOp",EDGE,"E8.19.1"),sQuery(id+"F0.wireOp",EDGE,"E10")])],"isStart":false});
            var sketch = newSketch(context, id + "F3", { "sketchPlane" : qUnion([Q0])});
            skArc(sketch, "E18.0", {"start": v(12.17, 49.68) * mm, "mid": v(11.38, 49.87) * mm, "end": v(10.59, 50.04) * mm});
            skArc(sketch, "E19.0", {"start": v(6.68, 36.9) * mm, "mid": v(7.48, 36.75) * mm, "end": v(8.28, 36.57) * mm});
            skLineSegment(sketch, "E20", {"start": v(10.59, 50.04) * mm, "end": v(6.68, 36.9) * mm});
            skLineSegment(sketch, "E21", {"start": v(8.28, 36.57) * mm, "end": v(12.17, 49.68) * mm});
            skLineSegment(sketch, "E22", {"start": v(5.4, 50.86) * mm, "end": v(5.05, 37.16) * mm});
            skLineSegment(sketch, "E23", {"start": v(3.43, 37.34) * mm, "end": v(3.77, 51.01) * mm});
            skArc(sketch, "E24.trimOffspring", {"start": v(3.43, 37.34) * mm, "mid": v(4.24, 37.26) * mm, "end": v(5.05, 37.16) * mm});
            skArc(sketch, "E25.trimOffspring", {"start": v(5.4, 50.86) * mm, "mid": v(4.58, 50.94) * mm, "end": v(3.77, 51.01) * mm});
            skArc(sketch, "E26.1.0", {"start": v(34.26, 37.98) * mm, "mid": v(33.65, 38.52) * mm, "end": v(33.04, 39.05) * mm});
            skLineSegment(sketch, "E26.1.1", {"start": v(34.26, 37.98) * mm, "end": v(25.93, 27.1) * mm});
            skLineSegment(sketch, "E26.1.2", {"start": v(28.2, 24.72) * mm, "end": v(39.05, 33.04) * mm});
            skArc(sketch, "E26.1.3", {"start": v(24.72, 28.2) * mm, "mid": v(25.33, 27.65) * mm, "end": v(25.93, 27.1) * mm});
            skLineSegment(sketch, "E26.1.4", {"start": v(37.98, 34.26) * mm, "end": v(27.1, 25.93) * mm});
            skLineSegment(sketch, "E26.1.5", {"start": v(24.72, 28.2) * mm, "end": v(33.04, 39.05) * mm});
            skArc(sketch, "E26.1.6", {"start": v(27.1, 25.93) * mm, "mid": v(27.65, 25.33) * mm, "end": v(28.2, 24.72) * mm});
            skArc(sketch, "E26.1.7", {"start": v(39.05, 33.04) * mm, "mid": v(38.52, 33.65) * mm, "end": v(37.98, 34.26) * mm});
            skArc(sketch, "E26.2.0", {"start": v(50.04, 10.59) * mm, "mid": v(49.87, 11.38) * mm, "end": v(49.68, 12.17) * mm});
            skLineSegment(sketch, "E26.2.1", {"start": v(50.04, 10.59) * mm, "end": v(36.9, 6.68) * mm});
            skLineSegment(sketch, "E26.2.2", {"start": v(37.34, 3.43) * mm, "end": v(51.01, 3.77) * mm});
            skArc(sketch, "E26.2.3", {"start": v(36.57, 8.28) * mm, "mid": v(36.75, 7.48) * mm, "end": v(36.9, 6.68) * mm});
            skLineSegment(sketch, "E26.2.4", {"start": v(50.86, 5.4) * mm, "end": v(37.16, 5.05) * mm});
            skLineSegment(sketch, "E26.2.5", {"start": v(36.57, 8.28) * mm, "end": v(49.68, 12.17) * mm});
            skArc(sketch, "E26.2.6", {"start": v(37.16, 5.05) * mm, "mid": v(37.26, 4.24) * mm, "end": v(37.34, 3.43) * mm});
            skArc(sketch, "E26.2.7", {"start": v(51.01, 3.77) * mm, "mid": v(50.94, 4.58) * mm, "end": v(50.86, 5.4) * mm});
            skArc(sketch, "E26.3.0", {"start": v(46.7, -20.85) * mm, "mid": v(47.03, -20.1) * mm, "end": v(47.35, -19.35) * mm});
            skLineSegment(sketch, "E26.3.1", {"start": v(46.7, -20.85) * mm, "end": v(33.78, -16.29) * mm});
            skLineSegment(sketch, "E26.3.2", {"start": v(32.23, -19.18) * mm, "end": v(43.49, -26.93) * mm});
            skArc(sketch, "E26.3.3", {"start": v(34.46, -14.8) * mm, "mid": v(34.13, -15.55) * mm, "end": v(33.78, -16.29) * mm});
            skLineSegment(sketch, "E26.3.4", {"start": v(44.32, -25.53) * mm, "end": v(33.03, -17.76) * mm});
            skLineSegment(sketch, "E26.3.5", {"start": v(34.46, -14.8) * mm, "end": v(47.35, -19.35) * mm});
            skArc(sketch, "E26.3.6", {"start": v(33.03, -17.76) * mm, "mid": v(32.64, -18.47) * mm, "end": v(32.23, -19.18) * mm});
            skArc(sketch, "E26.3.7", {"start": v(43.49, -26.93) * mm, "mid": v(43.9, -26.24) * mm, "end": v(44.32, -25.53) * mm});
            skArc(sketch, "E26.4.0", {"start": v(25.53, -44.32) * mm, "mid": v(26.24, -43.9) * mm, "end": v(26.93, -43.49) * mm});
            skLineSegment(sketch, "E26.4.1", {"start": v(25.53, -44.32) * mm, "end": v(17.76, -33.03) * mm});
            skLineSegment(sketch, "E26.4.2", {"start": v(14.8, -34.46) * mm, "end": v(19.35, -47.35) * mm});
            skArc(sketch, "E26.4.3", {"start": v(19.18, -32.23) * mm, "mid": v(18.47, -32.64) * mm, "end": v(17.76, -33.03) * mm});
            skLineSegment(sketch, "E26.4.4", {"start": v(20.85, -46.7) * mm, "end": v(16.29, -33.78) * mm});
            skLineSegment(sketch, "E26.4.5", {"start": v(19.18, -32.23) * mm, "end": v(26.93, -43.49) * mm});
            skArc(sketch, "E26.4.6", {"start": v(16.29, -33.78) * mm, "mid": v(15.55, -34.13) * mm, "end": v(14.8, -34.46) * mm});
            skArc(sketch, "E26.4.7", {"start": v(19.35, -47.35) * mm, "mid": v(20.1, -47.03) * mm, "end": v(20.85, -46.7) * mm});
            skArc(sketch, "E26.5.0", {"start": v(-5.4, -50.86) * mm, "mid": v(-4.58, -50.94) * mm, "end": v(-3.77, -51.01) * mm});
            skLineSegment(sketch, "E26.5.1", {"start": v(-5.4, -50.86) * mm, "end": v(-5.05, -37.16) * mm});
            skLineSegment(sketch, "E26.5.2", {"start": v(-8.28, -36.57) * mm, "end": v(-12.17, -49.68) * mm});
            skArc(sketch, "E26.5.3", {"start": v(-3.43, -37.34) * mm, "mid": v(-4.24, -37.26) * mm, "end": v(-5.05, -37.16) * mm});
            skLineSegment(sketch, "E26.5.4", {"start": v(-10.59, -50.04) * mm, "end": v(-6.68, -36.9) * mm});
            skLineSegment(sketch, "E26.5.5", {"start": v(-3.43, -37.34) * mm, "end": v(-3.77, -51.01) * mm});
            skArc(sketch, "E26.5.6", {"start": v(-6.68, -36.9) * mm, "mid": v(-7.48, -36.75) * mm, "end": v(-8.28, -36.57) * mm});
            skArc(sketch, "E26.5.7", {"start": v(-12.17, -49.68) * mm, "mid": v(-11.38, -49.87) * mm, "end": v(-10.59, -50.04) * mm});
            skArc(sketch, "E26.6.0", {"start": v(-34.26, -37.98) * mm, "mid": v(-33.65, -38.52) * mm, "end": v(-33.04, -39.05) * mm});
            skLineSegment(sketch, "E26.6.1", {"start": v(-34.26, -37.98) * mm, "end": v(-25.93, -27.1) * mm});
            skLineSegment(sketch, "E26.6.2", {"start": v(-28.2, -24.72) * mm, "end": v(-39.05, -33.04) * mm});
            skArc(sketch, "E26.6.3", {"start": v(-24.72, -28.2) * mm, "mid": v(-25.33, -27.65) * mm, "end": v(-25.93, -27.1) * mm});
            skLineSegment(sketch, "E26.6.4", {"start": v(-37.98, -34.26) * mm, "end": v(-27.1, -25.93) * mm});
            skLineSegment(sketch, "E26.6.5", {"start": v(-24.72, -28.2) * mm, "end": v(-33.04, -39.05) * mm});
            skArc(sketch, "E26.6.6", {"start": v(-27.1, -25.93) * mm, "mid": v(-27.65, -25.33) * mm, "end": v(-28.2, -24.72) * mm});
            skArc(sketch, "E26.6.7", {"start": v(-39.05, -33.04) * mm, "mid": v(-38.52, -33.65) * mm, "end": v(-37.98, -34.26) * mm});
            skArc(sketch, "E26.7.0", {"start": v(-50.04, -10.59) * mm, "mid": v(-49.87, -11.38) * mm, "end": v(-49.68, -12.17) * mm});
            skLineSegment(sketch, "E26.7.1", {"start": v(-50.04, -10.59) * mm, "end": v(-36.9, -6.68) * mm});
            skLineSegment(sketch, "E26.7.2", {"start": v(-37.34, -3.43) * mm, "end": v(-51.01, -3.77) * mm});
            skArc(sketch, "E26.7.3", {"start": v(-36.57, -8.28) * mm, "mid": v(-36.75, -7.48) * mm, "end": v(-36.9, -6.68) * mm});
            skLineSegment(sketch, "E26.7.4", {"start": v(-50.86, -5.4) * mm, "end": v(-37.16, -5.05) * mm});
            skLineSegment(sketch, "E26.7.5", {"start": v(-36.57, -8.28) * mm, "end": v(-49.68, -12.17) * mm});
            skArc(sketch, "E26.7.6", {"start": v(-37.16, -5.05) * mm, "mid": v(-37.26, -4.24) * mm, "end": v(-37.34, -3.43) * mm});
            skArc(sketch, "E26.7.7", {"start": v(-51.01, -3.77) * mm, "mid": v(-50.94, -4.58) * mm, "end": v(-50.86, -5.4) * mm});
            skArc(sketch, "E26.8.0", {"start": v(-46.7, 20.85) * mm, "mid": v(-47.03, 20.1) * mm, "end": v(-47.35, 19.35) * mm});
            skLineSegment(sketch, "E26.8.1", {"start": v(-46.7, 20.85) * mm, "end": v(-33.78, 16.29) * mm});
            skLineSegment(sketch, "E26.8.2", {"start": v(-32.23, 19.18) * mm, "end": v(-43.49, 26.93) * mm});
            skArc(sketch, "E26.8.3", {"start": v(-34.46, 14.8) * mm, "mid": v(-34.13, 15.55) * mm, "end": v(-33.78, 16.29) * mm});
            skLineSegment(sketch, "E26.8.4", {"start": v(-44.32, 25.53) * mm, "end": v(-33.03, 17.76) * mm});
            skLineSegment(sketch, "E26.8.5", {"start": v(-34.46, 14.8) * mm, "end": v(-47.35, 19.35) * mm});
            skArc(sketch, "E26.8.6", {"start": v(-33.03, 17.76) * mm, "mid": v(-32.64, 18.47) * mm, "end": v(-32.23, 19.18) * mm});
            skArc(sketch, "E26.8.7", {"start": v(-43.49, 26.93) * mm, "mid": v(-43.9, 26.24) * mm, "end": v(-44.32, 25.53) * mm});
            skArc(sketch, "E26.9.0", {"start": v(-25.53, 44.32) * mm, "mid": v(-26.24, 43.9) * mm, "end": v(-26.93, 43.49) * mm});
            skLineSegment(sketch, "E26.9.1", {"start": v(-25.53, 44.32) * mm, "end": v(-17.76, 33.03) * mm});
            skLineSegment(sketch, "E26.9.2", {"start": v(-14.8, 34.46) * mm, "end": v(-19.35, 47.35) * mm});
            skArc(sketch, "E26.9.3", {"start": v(-19.18, 32.23) * mm, "mid": v(-18.47, 32.64) * mm, "end": v(-17.76, 33.03) * mm});
            skLineSegment(sketch, "E26.9.4", {"start": v(-20.85, 46.7) * mm, "end": v(-16.29, 33.78) * mm});
            skLineSegment(sketch, "E26.9.5", {"start": v(-19.18, 32.23) * mm, "end": v(-26.93, 43.49) * mm});
            skArc(sketch, "E26.9.6", {"start": v(-16.29, 33.78) * mm, "mid": v(-15.55, 34.13) * mm, "end": v(-14.8, 34.46) * mm});
            skArc(sketch, "E26.9.7", {"start": v(-19.35, 47.35) * mm, "mid": v(-20.1, 47.03) * mm, "end": v(-20.85, 46.7) * mm});
            skLineSegment(sketch, "E26.anchor1", {"start": v(0, 0) * mm, "end": v(3.43, 37.34) * mm, "construction": true});
            skLineSegment(sketch, "E26.anchor2", {"start": v(0, 0) * mm, "end": v(-19.18, 32.23) * mm, "construction": true});
            skSolve(sketch);
        }
        {
            var Q0;
            Q0=makeQuery(id+"F3.imprint","IMPRINT",FACE,{"disambiguationData":[TD([[makeQuery(id+"F3.imprint","IMPRINT",EDGE,{"derivedFrom":sQuery(id+"F3.wireOp",EDGE,"E26.8.0")}),1.0]])]});
            var Q1;
            Q1=makeQuery(id+"F3.imprint","IMPRINT",FACE,{"disambiguationData":[TD([[makeQuery(id+"F3.imprint","IMPRINT",EDGE,{"derivedFrom":sQuery(id+"F3.wireOp",EDGE,"E26.8.2")}),1.0]])]});
            var Q2;
            Q2=makeQuery(id+"F3.imprint","IMPRINT",FACE,{"disambiguationData":[TD([[makeQuery(id+"F3.imprint","IMPRINT",EDGE,{"derivedFrom":sQuery(id+"F3.wireOp",EDGE,"E26.9.0")}),1.0]])]});
            var Q3;
            Q3=makeQuery(id+"F3.imprint","IMPRINT",FACE,{"disambiguationData":[TD([[makeQuery(id+"F3.imprint","IMPRINT",EDGE,{"derivedFrom":sQuery(id+"F3.wireOp",EDGE,"E26.9.2")}),1.0]])]});
            var Q4;
            Q4=makeQuery(id+"F3.imprint","IMPRINT",FACE,{"disambiguationData":[TD([[makeQuery(id+"F3.imprint","IMPRINT",EDGE,{"derivedFrom":sQuery(id+"F3.wireOp",EDGE,"E22")}),-1.0]])]});
            var Q5;
            Q5=makeQuery(id+"F3.imprint","IMPRINT",FACE,{"disambiguationData":[TD([[makeQuery(id+"F3.imprint","IMPRINT",EDGE,{"derivedFrom":sQuery(id+"F3.wireOp",EDGE,"E18.0")}),1.0]])]});
            var Q6;
            Q6=makeQuery(id+"F3.imprint","IMPRINT",FACE,{"disambiguationData":[TD([[makeQuery(id+"F3.imprint","IMPRINT",EDGE,{"derivedFrom":sQuery(id+"F3.wireOp",EDGE,"E26.1.0")}),1.0]])]});
            var Q7;
            Q7=makeQuery(id+"F3.imprint","IMPRINT",FACE,{"disambiguationData":[TD([[makeQuery(id+"F3.imprint","IMPRINT",EDGE,{"derivedFrom":sQuery(id+"F3.wireOp",EDGE,"E26.1.2")}),1.0]])]});
            var Q8;
            Q8=makeQuery(id+"F3.imprint","IMPRINT",FACE,{"disambiguationData":[TD([[makeQuery(id+"F3.imprint","IMPRINT",EDGE,{"derivedFrom":sQuery(id+"F3.wireOp",EDGE,"E26.2.0")}),1.0]])]});
            var Q9;
            Q9=makeQuery(id+"F3.imprint","IMPRINT",FACE,{"disambiguationData":[TD([[makeQuery(id+"F3.imprint","IMPRINT",EDGE,{"derivedFrom":sQuery(id+"F3.wireOp",EDGE,"E26.2.2")}),1.0]])]});
            var Q10;
            Q10=makeQuery(id+"F3.imprint","IMPRINT",FACE,{"disambiguationData":[TD([[makeQuery(id+"F3.imprint","IMPRINT",EDGE,{"derivedFrom":sQuery(id+"F3.wireOp",EDGE,"E26.3.0")}),1.0]])]});
            var Q11;
            Q11=makeQuery(id+"F3.imprint","IMPRINT",FACE,{"disambiguationData":[TD([[makeQuery(id+"F3.imprint","IMPRINT",EDGE,{"derivedFrom":sQuery(id+"F3.wireOp",EDGE,"E26.3.2")}),1.0]])]});
            var Q12;
            Q12=makeQuery(id+"F3.imprint","IMPRINT",FACE,{"disambiguationData":[TD([[makeQuery(id+"F3.imprint","IMPRINT",EDGE,{"derivedFrom":sQuery(id+"F3.wireOp",EDGE,"E26.4.0")}),1.0]])]});
            var Q13;
            Q13=makeQuery(id+"F3.imprint","IMPRINT",FACE,{"disambiguationData":[TD([[makeQuery(id+"F3.imprint","IMPRINT",EDGE,{"derivedFrom":sQuery(id+"F3.wireOp",EDGE,"E26.4.2")}),1.0]])]});
            var Q14;
            Q14=makeQuery(id+"F3.imprint","IMPRINT",FACE,{"disambiguationData":[TD([[makeQuery(id+"F3.imprint","IMPRINT",EDGE,{"derivedFrom":sQuery(id+"F3.wireOp",EDGE,"E26.5.0")}),1.0]])]});
            var Q15;
            Q15=makeQuery(id+"F3.imprint","IMPRINT",FACE,{"disambiguationData":[TD([[makeQuery(id+"F3.imprint","IMPRINT",EDGE,{"derivedFrom":sQuery(id+"F3.wireOp",EDGE,"E26.5.2")}),1.0]])]});
            var Q16;
            Q16=makeQuery(id+"F3.imprint","IMPRINT",FACE,{"disambiguationData":[TD([[makeQuery(id+"F3.imprint","IMPRINT",EDGE,{"derivedFrom":sQuery(id+"F3.wireOp",EDGE,"E26.6.0")}),1.0]])]});
            var Q17;
            Q17=makeQuery(id+"F3.imprint","IMPRINT",FACE,{"disambiguationData":[TD([[makeQuery(id+"F3.imprint","IMPRINT",EDGE,{"derivedFrom":sQuery(id+"F3.wireOp",EDGE,"E26.6.2")}),1.0]])]});
            var Q18;
            Q18=makeQuery(id+"F3.imprint","IMPRINT",FACE,{"disambiguationData":[TD([[makeQuery(id+"F3.imprint","IMPRINT",EDGE,{"derivedFrom":sQuery(id+"F3.wireOp",EDGE,"E26.7.0")}),1.0]])]});
            var Q19;
            Q19=makeQuery(id+"F3.imprint","IMPRINT",FACE,{"disambiguationData":[TD([[makeQuery(id+"F3.imprint","IMPRINT",EDGE,{"derivedFrom":sQuery(id+"F3.wireOp",EDGE,"E26.7.2")}),1.0]])]});
            extrude(context, id + "F4", {"entities" : qUnion([Q0, Q1, Q2, Q3, Q4, Q5, Q6, Q7, Q8, Q9, Q10, Q11, Q12, Q13, Q14, Q15, Q16, Q17, Q18, Q19]), "operationType" : NewBodyOperationType.ADD, "depth" : 2 * mm, "offsetDistance" : 25 * mm});
        }
        {
            var Q0;
            {var subQ0=sQuery(id+"F0.wireOp",EDGE,"E10");var subQ1=sQuery(id+"F0.wireOp",EDGE,"E8.5.1");var subQ2=sQuery(id+"F0.wireOp",EDGE,"E8.4.1");var subQ3=sQuery(id+"F0.wireOp",EDGE,"E5.5.4");var subQ4=sQuery(id+"F0.wireOp",EDGE,"E8.3.1");var subQ5=sQuery(id+"F0.wireOp",EDGE,"E5.5.3");var subQ6=sQuery(id+"F0.wireOp",EDGE,"E5.5.7");var subQ7=sQuery(id+"F0.wireOp",EDGE,"E5.5.6");var subQ8=sQuery(id+"F0.wireOp",EDGE,"E5.5.5");var subQ9=sQuery(id+"F0.wireOp",EDGE,"E5.4.5");var subQ10=sQuery(id+"F0.wireOp",EDGE,"E5.4.6");var subQ11=sQuery(id+"F0.wireOp",EDGE,"E5.4.7");var subQ12=sQuery(id+"F0.wireOp",EDGE,"E5.4.3");var subQ13=sQuery(id+"F0.wireOp",EDGE,"E5.4.4");Q0=makeQuery(id+"F4.boolean.opBoolean","SPLIT",FACE,{"disambiguationData":[TD([makeQuery(id+"F1.opExtrude","SWEPT_FACE",FACE,{"disambiguationData":[OSD([subQ12])]})])],"derivedFrom":makeQuery(id+"F1.opExtrude","CAP_FACE",FACE,{"disambiguationData":[OSD([sQuery(id+"F0.wireOp",EDGE,"E0.bottom"),sQuery(id+"F0.wireOp",EDGE,"E0.left"),sQuery(id+"F0.wireOp",EDGE,"E0.right"),sQuery(id+"F0.wireOp",EDGE,"E2"),sQuery(id+"F0.wireOp",EDGE,"E3"),sQuery(id+"F0.wireOp",EDGE,"E5.1.3"),sQuery(id+"F0.wireOp",EDGE,"E5.1.4"),sQuery(id+"F0.wireOp",EDGE,"E5.1.5"),sQuery(id+"F0.wireOp",EDGE,"E5.1.6"),sQuery(id+"F0.wireOp",EDGE,"E5.1.7"),sQuery(id+"F0.wireOp",EDGE,"E5.2.3"),sQuery(id+"F0.wireOp",EDGE,"E5.2.4"),sQuery(id+"F0.wireOp",EDGE,"E5.2.5"),sQuery(id+"F0.wireOp",EDGE,"E5.2.6"),sQuery(id+"F0.wireOp",EDGE,"E5.2.7"),sQuery(id+"F0.wireOp",EDGE,"E5.3.3"),sQuery(id+"F0.wireOp",EDGE,"E5.3.4"),sQuery(id+"F0.wireOp",EDGE,"E5.3.5"),sQuery(id+"F0.wireOp",EDGE,"E5.3.6"),sQuery(id+"F0.wireOp",EDGE,"E5.3.7"),subQ12,subQ13,subQ9,subQ10,subQ11,subQ5,subQ3,subQ8,subQ7,subQ6,sQuery(id+"F0.wireOp",EDGE,"E5.6.3"),sQuery(id+"F0.wireOp",EDGE,"E5.6.4"),sQuery(id+"F0.wireOp",EDGE,"E5.6.5"),sQuery(id+"F0.wireOp",EDGE,"E5.6.6"),sQuery(id+"F0.wireOp",EDGE,"E5.6.7"),sQuery(id+"F0.wireOp",EDGE,"E5.7.3"),sQuery(id+"F0.wireOp",EDGE,"E5.7.4"),sQuery(id+"F0.wireOp",EDGE,"E5.7.5"),sQuery(id+"F0.wireOp",EDGE,"E5.7.6"),sQuery(id+"F0.wireOp",EDGE,"E5.7.7"),sQuery(id+"F0.wireOp",EDGE,"E5.8.3"),sQuery(id+"F0.wireOp",EDGE,"E5.8.4"),sQuery(id+"F0.wireOp",EDGE,"E5.8.5"),sQuery(id+"F0.wireOp",EDGE,"E5.8.6"),sQuery(id+"F0.wireOp",EDGE,"E5.8.7"),sQuery(id+"F0.wireOp",EDGE,"E5.9.3"),sQuery(id+"F0.wireOp",EDGE,"E5.9.4"),sQuery(id+"F0.wireOp",EDGE,"E5.9.5"),sQuery(id+"F0.wireOp",EDGE,"E5.9.6"),sQuery(id+"F0.wireOp",EDGE,"E5.9.7"),sQuery(id+"F0.wireOp",EDGE,"E5.10.3"),sQuery(id+"F0.wireOp",EDGE,"E5.10.4"),sQuery(id+"F0.wireOp",EDGE,"E5.10.5"),sQuery(id+"F0.wireOp",EDGE,"E5.10.6"),sQuery(id+"F0.wireOp",EDGE,"E5.10.7"),sQuery(id+"F0.wireOp",EDGE,"E5.11.3"),sQuery(id+"F0.wireOp",EDGE,"E5.11.4"),sQuery(id+"F0.wireOp",EDGE,"E5.11.5"),sQuery(id+"F0.wireOp",EDGE,"E5.11.6"),sQuery(id+"F0.wireOp",EDGE,"E5.11.7"),sQuery(id+"F0.wireOp",EDGE,"E5.12.3"),sQuery(id+"F0.wireOp",EDGE,"E5.12.4"),sQuery(id+"F0.wireOp",EDGE,"E5.12.5"),sQuery(id+"F0.wireOp",EDGE,"E5.12.6"),sQuery(id+"F0.wireOp",EDGE,"E5.12.7"),sQuery(id+"F0.wireOp",EDGE,"E5.13.3"),sQuery(id+"F0.wireOp",EDGE,"E5.13.4"),sQuery(id+"F0.wireOp",EDGE,"E5.13.5"),sQuery(id+"F0.wireOp",EDGE,"E5.13.6"),sQuery(id+"F0.wireOp",EDGE,"E5.13.7"),sQuery(id+"F0.wireOp",EDGE,"E5.14.3"),sQuery(id+"F0.wireOp",EDGE,"E5.14.4"),sQuery(id+"F0.wireOp",EDGE,"E5.14.5"),sQuery(id+"F0.wireOp",EDGE,"E5.14.6"),sQuery(id+"F0.wireOp",EDGE,"E5.14.7"),sQuery(id+"F0.wireOp",EDGE,"E5.15.3"),sQuery(id+"F0.wireOp",EDGE,"E5.15.4"),sQuery(id+"F0.wireOp",EDGE,"E5.15.5"),sQuery(id+"F0.wireOp",EDGE,"E5.15.6"),sQuery(id+"F0.wireOp",EDGE,"E5.15.7"),sQuery(id+"F0.wireOp",EDGE,"E5.16.3"),sQuery(id+"F0.wireOp",EDGE,"E5.16.4"),sQuery(id+"F0.wireOp",EDGE,"E5.16.5"),sQuery(id+"F0.wireOp",EDGE,"E5.16.6"),sQuery(id+"F0.wireOp",EDGE,"E5.16.7"),sQuery(id+"F0.wireOp",EDGE,"E5.17.3"),sQuery(id+"F0.wireOp",EDGE,"E5.17.4"),sQuery(id+"F0.wireOp",EDGE,"E5.17.5"),sQuery(id+"F0.wireOp",EDGE,"E5.17.6"),sQuery(id+"F0.wireOp",EDGE,"E5.17.7"),sQuery(id+"F0.wireOp",EDGE,"E5.18.3"),sQuery(id+"F0.wireOp",EDGE,"E5.18.4"),sQuery(id+"F0.wireOp",EDGE,"E5.18.5"),sQuery(id+"F0.wireOp",EDGE,"E5.18.6"),sQuery(id+"F0.wireOp",EDGE,"E5.18.7"),sQuery(id+"F0.wireOp",EDGE,"E5.19.3"),sQuery(id+"F0.wireOp",EDGE,"E5.19.4"),sQuery(id+"F0.wireOp",EDGE,"E5.19.5"),sQuery(id+"F0.wireOp",EDGE,"E5.19.6"),sQuery(id+"F0.wireOp",EDGE,"E5.19.7"),sQuery(id+"F0.wireOp",EDGE,"E7"),sQuery(id+"F0.wireOp",EDGE,"E8.1.1"),sQuery(id+"F0.wireOp",EDGE,"E8.2.1"),subQ4,subQ2,subQ1,sQuery(id+"F0.wireOp",EDGE,"E8.6.1"),sQuery(id+"F0.wireOp",EDGE,"E8.7.1"),sQuery(id+"F0.wireOp",EDGE,"E8.8.1"),sQuery(id+"F0.wireOp",EDGE,"E8.9.1"),sQuery(id+"F0.wireOp",EDGE,"E8.10.1"),sQuery(id+"F0.wireOp",EDGE,"E8.11.1"),sQuery(id+"F0.wireOp",EDGE,"E8.12.1"),sQuery(id+"F0.wireOp",EDGE,"E8.13.1"),sQuery(id+"F0.wireOp",EDGE,"E8.14.1"),sQuery(id+"F0.wireOp",EDGE,"E8.15.1"),sQuery(id+"F0.wireOp",EDGE,"E8.16.1"),sQuery(id+"F0.wireOp",EDGE,"E8.17.1"),sQuery(id+"F0.wireOp",EDGE,"E8.18.1"),sQuery(id+"F0.wireOp",EDGE,"E8.19.1"),subQ0])],"isStart":false})});}
            var sketch = newSketch(context, id + "F5", { "sketchPlane" : qUnion([Q0])});
            skArc(sketch, "E27.0.0", {"start": v(-37.34, -3.43) * mm, "mid": v(-37.04, 5.87) * mm, "end": v(-34.46, 14.8) * mm, "construction": true});
            skLineSegment(sketch, "E27.0.1", {"start": v(-34.46, 14.8) * mm, "end": v(-47.35, 19.35) * mm, "construction": true});
            skArc(sketch, "E27.0.2", {"start": v(-47.35, 19.35) * mm, "mid": v(-47.54, 18.89) * mm, "end": v(-47.72, 18.42) * mm, "construction": true});
            skLineSegment(sketch, "E27.0.3", {"start": v(-47.72, 18.42) * mm, "end": v(-46.2, 16.88) * mm, "construction": true});
            skLineSegment(sketch, "E27.0.4", {"start": v(-46.2, 16.88) * mm, "end": v(-42.2, 15.58) * mm, "construction": true});
            skLineSegment(sketch, "E27.0.5", {"start": v(-42.2, 15.58) * mm, "end": v(-43.3, 12.2) * mm, "construction": true});
            skLineSegment(sketch, "E27.0.6", {"start": v(-43.3, 12.2) * mm, "end": v(-47.3, 13.5) * mm, "construction": true});
            skLineSegment(sketch, "E27.0.7", {"start": v(-47.3, 13.5) * mm, "end": v(-49.43, 13.14) * mm, "construction": true});
            skArc(sketch, "E27.0.8", {"start": v(-49.43, 13.14) * mm, "mid": v(-50.52, 8) * mm, "end": v(-51.07, 2.77) * mm, "construction": true});
            skLineSegment(sketch, "E27.0.9", {"start": v(-51.07, 2.78) * mm, "end": v(-49.15, 1.77) * mm, "construction": true});
            skLineSegment(sketch, "E27.0.10", {"start": v(-49.15, 1.77) * mm, "end": v(-44.95, 1.77) * mm, "construction": true});
            skLineSegment(sketch, "E27.0.11", {"start": v(-44.95, 1.77) * mm, "end": v(-44.95, -1.78) * mm, "construction": true});
            skLineSegment(sketch, "E27.0.12", {"start": v(-44.95, -1.78) * mm, "end": v(-49.15, -1.78) * mm, "construction": true});
            skLineSegment(sketch, "E27.0.13", {"start": v(-49.15, -1.78) * mm, "end": v(-51.07, -2.78) * mm, "construction": true});
            skArc(sketch, "E27.0.14", {"start": v(-51.07, -2.78) * mm, "mid": v(-51.05, -3.27) * mm, "end": v(-51.01, -3.77) * mm, "construction": true});
            skLineSegment(sketch, "E27.0.15", {"start": v(-51.01, -3.77) * mm, "end": v(-37.34, -3.43) * mm, "construction": true});
            skLineSegment(sketch, "E28", {"start": v(-37.78, 12.28) * mm, "end": v(-40.63, 13.2) * mm});
            skLineSegment(sketch, "E29", {"start": v(-39.72, 0) * mm, "end": v(-42.72, 0) * mm});
            skArc(sketch, "E30", {"start": v(-37.78, 12.28) * mm, "mid": v(-38.74, 14.17) * mm, "end": v(-40.63, 13.2) * mm});
            skArc(sketch, "E31", {"start": v(-39.72, 0) * mm, "mid": v(-41.22, 1.5) * mm, "end": v(-42.72, 0) * mm});
            skPoint(sketch, "E32.orphan", {"position": v(-42.75, 13.9) * mm});
            skPoint(sketch, "E33.orphan", {"position": v(-35.66, 11.59) * mm});
            skPoint(sketch, "E34.orphan", {"position": v(-37.5, 0) * mm});
            skPoint(sketch, "E35.orphan", {"position": v(-44.95, 0) * mm});
            skSolve(sketch);
        }
        {
            var Q0;
            Q0=makeQuery(id+"F5.imprint","IMPRINT",FACE,{"disambiguationData":[TD([[makeQuery(id+"F5.imprint","IMPRINT",EDGE,{"derivedFrom":sQuery(id+"F5.wireOp",EDGE,"E28")}),-1.0]])]});
            var Q1;
            Q1=sQuery(id+"F5.wireOp",EDGE,"E28");
            revolve(context, id + "F6", {"entities" : qUnion([Q0]), "axis" : qUnion([Q1]), "revolveType" : RevolveType.FULL, "oppositeDirection" : true});
        }
        {
            var Q0;
            Q0=makeQuery(id+"F5.imprint","IMPRINT",FACE,{"disambiguationData":[TD([[makeQuery(id+"F5.imprint","IMPRINT",EDGE,{"derivedFrom":sQuery(id+"F5.wireOp",EDGE,"E29")}),-1.0]])]});
            var Q1;
            Q1=sQuery(id+"F5.wireOp",EDGE,"E29");
            revolve(context, id + "F7", {"entities" : qUnion([Q0]), "axis" : qUnion([Q1]), "revolveType" : RevolveType.FULL});
        }
        {
            var Q0;
            Q0=qCreatedBy(makeId("Right.planeOp"),FACE);
            var sketch = newSketch(context, id + "F8", { "sketchPlane" : qUnion([Q0])});
            skLineSegment(sketch, "E36", {"start": v(0, 0) * mm, "end": v(0, -5.23) * mm, "construction": true});
            skSolve(sketch);
        }
        {
            var Q0;
            Q0=makeQuery(id+"F6.opRevolve","SWEPT_BODY",BODY,{"disambiguationData":[OSD([sQuery(id+"F5.wireOp",EDGE,"E28"),sQuery(id+"F5.wireOp",EDGE,"E30")])]});
            var Q1;
            Q1=makeQuery(id+"F7.opRevolve","SWEPT_BODY",BODY,{"disambiguationData":[OSD([sQuery(id+"F5.wireOp",EDGE,"E29"),sQuery(id+"F5.wireOp",EDGE,"E31")])]});
            var Q2;
            Q2=sQuery(id+"F8.wireOp",EDGE,"E36");
            circularPattern(context, id + "F9", {"entities" : qUnion([Q0, Q1]), "axis" : qUnion([Q2]), "angle" : 360 * degree, "instanceCount" : 10, "equalSpace" : true});
        }
        {
            var Q0;
            Q0=makeQuery(id+"F9.opPattern","COPY",BODY,{"derivedFrom":makeQuery(id+"F6.opRevolve","SWEPT_BODY",BODY,{"disambiguationData":[OSD([sQuery(id+"F5.wireOp",EDGE,"E28"),sQuery(id+"F5.wireOp",EDGE,"E30")])]}),"instanceName":"8"});
            var Q1;
            Q1=makeQuery(id+"F9.opPattern","COPY",BODY,{"derivedFrom":makeQuery(id+"F7.opRevolve","SWEPT_BODY",BODY,{"disambiguationData":[OSD([sQuery(id+"F5.wireOp",EDGE,"E29"),sQuery(id+"F5.wireOp",EDGE,"E31")])]}),"instanceName":"8"});
            var Q2;
            Q2=makeQuery(id+"F9.opPattern","COPY",BODY,{"derivedFrom":makeQuery(id+"F7.opRevolve","SWEPT_BODY",BODY,{"disambiguationData":[OSD([sQuery(id+"F5.wireOp",EDGE,"E29"),sQuery(id+"F5.wireOp",EDGE,"E31")])]}),"instanceName":"7"});
            var Q3;
            Q3=makeQuery(id+"F9.opPattern","COPY",BODY,{"derivedFrom":makeQuery(id+"F6.opRevolve","SWEPT_BODY",BODY,{"disambiguationData":[OSD([sQuery(id+"F5.wireOp",EDGE,"E28"),sQuery(id+"F5.wireOp",EDGE,"E30")])]}),"instanceName":"7"});
            var Q4;
            Q4=makeQuery(id+"F9.opPattern","COPY",BODY,{"derivedFrom":makeQuery(id+"F7.opRevolve","SWEPT_BODY",BODY,{"disambiguationData":[OSD([sQuery(id+"F5.wireOp",EDGE,"E29"),sQuery(id+"F5.wireOp",EDGE,"E31")])]}),"instanceName":"6"});
            var Q5;
            Q5=makeQuery(id+"F9.opPattern","COPY",BODY,{"derivedFrom":makeQuery(id+"F6.opRevolve","SWEPT_BODY",BODY,{"disambiguationData":[OSD([sQuery(id+"F5.wireOp",EDGE,"E28"),sQuery(id+"F5.wireOp",EDGE,"E30")])]}),"instanceName":"6"});
            var Q6;
            Q6=makeQuery(id+"F9.opPattern","COPY",BODY,{"derivedFrom":makeQuery(id+"F7.opRevolve","SWEPT_BODY",BODY,{"disambiguationData":[OSD([sQuery(id+"F5.wireOp",EDGE,"E29"),sQuery(id+"F5.wireOp",EDGE,"E31")])]}),"instanceName":"5"});
            var Q7;
            Q7=makeQuery(id+"F9.opPattern","COPY",BODY,{"derivedFrom":makeQuery(id+"F6.opRevolve","SWEPT_BODY",BODY,{"disambiguationData":[OSD([sQuery(id+"F5.wireOp",EDGE,"E28"),sQuery(id+"F5.wireOp",EDGE,"E30")])]}),"instanceName":"5"});
            var Q8;
            Q8=makeQuery(id+"F9.opPattern","COPY",BODY,{"derivedFrom":makeQuery(id+"F7.opRevolve","SWEPT_BODY",BODY,{"disambiguationData":[OSD([sQuery(id+"F5.wireOp",EDGE,"E29"),sQuery(id+"F5.wireOp",EDGE,"E31")])]}),"instanceName":"4"});
            var Q9;
            Q9=makeQuery(id+"F9.opPattern","COPY",BODY,{"derivedFrom":makeQuery(id+"F6.opRevolve","SWEPT_BODY",BODY,{"disambiguationData":[OSD([sQuery(id+"F5.wireOp",EDGE,"E28"),sQuery(id+"F5.wireOp",EDGE,"E30")])]}),"instanceName":"4"});
            var Q10;
            Q10=makeQuery(id+"F9.opPattern","COPY",BODY,{"derivedFrom":makeQuery(id+"F7.opRevolve","SWEPT_BODY",BODY,{"disambiguationData":[OSD([sQuery(id+"F5.wireOp",EDGE,"E29"),sQuery(id+"F5.wireOp",EDGE,"E31")])]}),"instanceName":"3"});
            var Q11;
            Q11=makeQuery(id+"F9.opPattern","COPY",BODY,{"derivedFrom":makeQuery(id+"F6.opRevolve","SWEPT_BODY",BODY,{"disambiguationData":[OSD([sQuery(id+"F5.wireOp",EDGE,"E28"),sQuery(id+"F5.wireOp",EDGE,"E30")])]}),"instanceName":"3"});
            var Q12;
            Q12=makeQuery(id+"F9.opPattern","COPY",BODY,{"derivedFrom":makeQuery(id+"F7.opRevolve","SWEPT_BODY",BODY,{"disambiguationData":[OSD([sQuery(id+"F5.wireOp",EDGE,"E29"),sQuery(id+"F5.wireOp",EDGE,"E31")])]}),"instanceName":"2"});
            var Q13;
            Q13=makeQuery(id+"F9.opPattern","COPY",BODY,{"derivedFrom":makeQuery(id+"F6.opRevolve","SWEPT_BODY",BODY,{"disambiguationData":[OSD([sQuery(id+"F5.wireOp",EDGE,"E28"),sQuery(id+"F5.wireOp",EDGE,"E30")])]}),"instanceName":"2"});
            var Q14;
            Q14=makeQuery(id+"F9.opPattern","COPY",BODY,{"derivedFrom":makeQuery(id+"F7.opRevolve","SWEPT_BODY",BODY,{"disambiguationData":[OSD([sQuery(id+"F5.wireOp",EDGE,"E29"),sQuery(id+"F5.wireOp",EDGE,"E31")])]}),"instanceName":"1"});
            var Q15;
            Q15=makeQuery(id+"F9.opPattern","COPY",BODY,{"derivedFrom":makeQuery(id+"F6.opRevolve","SWEPT_BODY",BODY,{"disambiguationData":[OSD([sQuery(id+"F5.wireOp",EDGE,"E28"),sQuery(id+"F5.wireOp",EDGE,"E30")])]}),"instanceName":"1"});
            var Q16;
            Q16=makeQuery(id+"F7.opRevolve","SWEPT_BODY",BODY,{"disambiguationData":[OSD([sQuery(id+"F5.wireOp",EDGE,"E29"),sQuery(id+"F5.wireOp",EDGE,"E31")])]});
            var Q17;
            Q17=makeQuery(id+"F6.opRevolve","SWEPT_BODY",BODY,{"disambiguationData":[OSD([sQuery(id+"F5.wireOp",EDGE,"E28"),sQuery(id+"F5.wireOp",EDGE,"E30")])]});
            var Q18;
            Q18=makeQuery(id+"F9.opPattern","COPY",BODY,{"derivedFrom":makeQuery(id+"F7.opRevolve","SWEPT_BODY",BODY,{"disambiguationData":[OSD([sQuery(id+"F5.wireOp",EDGE,"E29"),sQuery(id+"F5.wireOp",EDGE,"E31")])]}),"instanceName":"9"});
            var Q19;
            Q19=makeQuery(id+"F9.opPattern","COPY",BODY,{"derivedFrom":makeQuery(id+"F6.opRevolve","SWEPT_BODY",BODY,{"disambiguationData":[OSD([sQuery(id+"F5.wireOp",EDGE,"E28"),sQuery(id+"F5.wireOp",EDGE,"E30")])]}),"instanceName":"9"});
            var Q20;
            Q20=makeQuery(id+"F1.opExtrude","SWEPT_BODY",BODY,{"disambiguationData":[OSD([sQuery(id+"F0.wireOp",EDGE,"E0.bottom"),sQuery(id+"F0.wireOp",EDGE,"E0.left"),sQuery(id+"F0.wireOp",EDGE,"E0.right"),sQuery(id+"F0.wireOp",EDGE,"E2"),sQuery(id+"F0.wireOp",EDGE,"E3"),sQuery(id+"F0.wireOp",EDGE,"E5.1.3"),sQuery(id+"F0.wireOp",EDGE,"E5.1.4"),sQuery(id+"F0.wireOp",EDGE,"E5.1.5"),sQuery(id+"F0.wireOp",EDGE,"E5.1.6"),sQuery(id+"F0.wireOp",EDGE,"E5.1.7"),sQuery(id+"F0.wireOp",EDGE,"E5.2.3"),sQuery(id+"F0.wireOp",EDGE,"E5.2.4"),sQuery(id+"F0.wireOp",EDGE,"E5.2.5"),sQuery(id+"F0.wireOp",EDGE,"E5.2.6"),sQuery(id+"F0.wireOp",EDGE,"E5.2.7"),sQuery(id+"F0.wireOp",EDGE,"E5.3.3"),sQuery(id+"F0.wireOp",EDGE,"E5.3.4"),sQuery(id+"F0.wireOp",EDGE,"E5.3.5"),sQuery(id+"F0.wireOp",EDGE,"E5.3.6"),sQuery(id+"F0.wireOp",EDGE,"E5.3.7"),sQuery(id+"F0.wireOp",EDGE,"E5.4.3"),sQuery(id+"F0.wireOp",EDGE,"E5.4.4"),sQuery(id+"F0.wireOp",EDGE,"E5.4.5"),sQuery(id+"F0.wireOp",EDGE,"E5.4.6"),sQuery(id+"F0.wireOp",EDGE,"E5.4.7"),sQuery(id+"F0.wireOp",EDGE,"E5.5.3"),sQuery(id+"F0.wireOp",EDGE,"E5.5.4"),sQuery(id+"F0.wireOp",EDGE,"E5.5.5"),sQuery(id+"F0.wireOp",EDGE,"E5.5.6"),sQuery(id+"F0.wireOp",EDGE,"E5.5.7"),sQuery(id+"F0.wireOp",EDGE,"E5.6.3"),sQuery(id+"F0.wireOp",EDGE,"E5.6.4"),sQuery(id+"F0.wireOp",EDGE,"E5.6.5"),sQuery(id+"F0.wireOp",EDGE,"E5.6.6"),sQuery(id+"F0.wireOp",EDGE,"E5.6.7"),sQuery(id+"F0.wireOp",EDGE,"E5.7.3"),sQuery(id+"F0.wireOp",EDGE,"E5.7.4"),sQuery(id+"F0.wireOp",EDGE,"E5.7.5"),sQuery(id+"F0.wireOp",EDGE,"E5.7.6"),sQuery(id+"F0.wireOp",EDGE,"E5.7.7"),sQuery(id+"F0.wireOp",EDGE,"E5.8.3"),sQuery(id+"F0.wireOp",EDGE,"E5.8.4"),sQuery(id+"F0.wireOp",EDGE,"E5.8.5"),sQuery(id+"F0.wireOp",EDGE,"E5.8.6"),sQuery(id+"F0.wireOp",EDGE,"E5.8.7"),sQuery(id+"F0.wireOp",EDGE,"E5.9.3"),sQuery(id+"F0.wireOp",EDGE,"E5.9.4"),sQuery(id+"F0.wireOp",EDGE,"E5.9.5"),sQuery(id+"F0.wireOp",EDGE,"E5.9.6"),sQuery(id+"F0.wireOp",EDGE,"E5.9.7"),sQuery(id+"F0.wireOp",EDGE,"E5.10.3"),sQuery(id+"F0.wireOp",EDGE,"E5.10.4"),sQuery(id+"F0.wireOp",EDGE,"E5.10.5"),sQuery(id+"F0.wireOp",EDGE,"E5.10.6"),sQuery(id+"F0.wireOp",EDGE,"E5.10.7"),sQuery(id+"F0.wireOp",EDGE,"E5.11.3"),sQuery(id+"F0.wireOp",EDGE,"E5.11.4"),sQuery(id+"F0.wireOp",EDGE,"E5.11.5"),sQuery(id+"F0.wireOp",EDGE,"E5.11.6"),sQuery(id+"F0.wireOp",EDGE,"E5.11.7"),sQuery(id+"F0.wireOp",EDGE,"E5.12.3"),sQuery(id+"F0.wireOp",EDGE,"E5.12.4"),sQuery(id+"F0.wireOp",EDGE,"E5.12.5"),sQuery(id+"F0.wireOp",EDGE,"E5.12.6"),sQuery(id+"F0.wireOp",EDGE,"E5.12.7"),sQuery(id+"F0.wireOp",EDGE,"E5.13.3"),sQuery(id+"F0.wireOp",EDGE,"E5.13.4"),sQuery(id+"F0.wireOp",EDGE,"E5.13.5"),sQuery(id+"F0.wireOp",EDGE,"E5.13.6"),sQuery(id+"F0.wireOp",EDGE,"E5.13.7"),sQuery(id+"F0.wireOp",EDGE,"E5.14.3"),sQuery(id+"F0.wireOp",EDGE,"E5.14.4"),sQuery(id+"F0.wireOp",EDGE,"E5.14.5"),sQuery(id+"F0.wireOp",EDGE,"E5.14.6"),sQuery(id+"F0.wireOp",EDGE,"E5.14.7"),sQuery(id+"F0.wireOp",EDGE,"E5.15.3"),sQuery(id+"F0.wireOp",EDGE,"E5.15.4"),sQuery(id+"F0.wireOp",EDGE,"E5.15.5"),sQuery(id+"F0.wireOp",EDGE,"E5.15.6"),sQuery(id+"F0.wireOp",EDGE,"E5.15.7"),sQuery(id+"F0.wireOp",EDGE,"E5.16.3"),sQuery(id+"F0.wireOp",EDGE,"E5.16.4"),sQuery(id+"F0.wireOp",EDGE,"E5.16.5"),sQuery(id+"F0.wireOp",EDGE,"E5.16.6"),sQuery(id+"F0.wireOp",EDGE,"E5.16.7"),sQuery(id+"F0.wireOp",EDGE,"E5.17.3"),sQuery(id+"F0.wireOp",EDGE,"E5.17.4"),sQuery(id+"F0.wireOp",EDGE,"E5.17.5"),sQuery(id+"F0.wireOp",EDGE,"E5.17.6"),sQuery(id+"F0.wireOp",EDGE,"E5.17.7"),sQuery(id+"F0.wireOp",EDGE,"E5.18.3"),sQuery(id+"F0.wireOp",EDGE,"E5.18.4"),sQuery(id+"F0.wireOp",EDGE,"E5.18.5"),sQuery(id+"F0.wireOp",EDGE,"E5.18.6"),sQuery(id+"F0.wireOp",EDGE,"E5.18.7"),sQuery(id+"F0.wireOp",EDGE,"E5.19.3"),sQuery(id+"F0.wireOp",EDGE,"E5.19.4"),sQuery(id+"F0.wireOp",EDGE,"E5.19.5"),sQuery(id+"F0.wireOp",EDGE,"E5.19.6"),sQuery(id+"F0.wireOp",EDGE,"E5.19.7"),sQuery(id+"F0.wireOp",EDGE,"E7"),sQuery(id+"F0.wireOp",EDGE,"E8.1.1"),sQuery(id+"F0.wireOp",EDGE,"E8.2.1"),sQuery(id+"F0.wireOp",EDGE,"E8.3.1"),sQuery(id+"F0.wireOp",EDGE,"E8.4.1"),sQuery(id+"F0.wireOp",EDGE,"E8.5.1"),sQuery(id+"F0.wireOp",EDGE,"E8.6.1"),sQuery(id+"F0.wireOp",EDGE,"E8.7.1"),sQuery(id+"F0.wireOp",EDGE,"E8.8.1"),sQuery(id+"F0.wireOp",EDGE,"E8.9.1"),sQuery(id+"F0.wireOp",EDGE,"E8.10.1"),sQuery(id+"F0.wireOp",EDGE,"E8.11.1"),sQuery(id+"F0.wireOp",EDGE,"E8.12.1"),sQuery(id+"F0.wireOp",EDGE,"E8.13.1"),sQuery(id+"F0.wireOp",EDGE,"E8.14.1"),sQuery(id+"F0.wireOp",EDGE,"E8.15.1"),sQuery(id+"F0.wireOp",EDGE,"E8.16.1"),sQuery(id+"F0.wireOp",EDGE,"E8.17.1"),sQuery(id+"F0.wireOp",EDGE,"E8.18.1"),sQuery(id+"F0.wireOp",EDGE,"E8.19.1"),sQuery(id+"F0.wireOp",EDGE,"E10")])]});
            booleanBodies(context, id + "F10", {"operationType" : BooleanOperationType.SUBTRACTION, "tools" : qUnion([Q0, Q1, Q2, Q3, Q4, Q5, Q6, Q7, Q8, Q9, Q10, Q11, Q12, Q13, Q14, Q15, Q16, Q17, Q18, Q19]), "targets" : qUnion([Q20]), "keepTools" : true});
        }
        {
            var Q0;
            Q0=makeQuery(id+"F6.opRevolve","SWEPT_BODY",BODY,{"disambiguationData":[OSD([sQuery(id+"F5.wireOp",EDGE,"E28"),sQuery(id+"F5.wireOp",EDGE,"E30")])]});
            var Q1;
            Q1=makeQuery(id+"F7.opRevolve","SWEPT_BODY",BODY,{"disambiguationData":[OSD([sQuery(id+"F5.wireOp",EDGE,"E29"),sQuery(id+"F5.wireOp",EDGE,"E31")])]});
            var Q2;
            Q2=makeQuery(id+"F9.opPattern","COPY",BODY,{"derivedFrom":makeQuery(id+"F6.opRevolve","SWEPT_BODY",BODY,{"disambiguationData":[OSD([sQuery(id+"F5.wireOp",EDGE,"E28"),sQuery(id+"F5.wireOp",EDGE,"E30")])]}),"instanceName":"1"});
            var Q3;
            Q3=makeQuery(id+"F9.opPattern","COPY",BODY,{"derivedFrom":makeQuery(id+"F7.opRevolve","SWEPT_BODY",BODY,{"disambiguationData":[OSD([sQuery(id+"F5.wireOp",EDGE,"E29"),sQuery(id+"F5.wireOp",EDGE,"E31")])]}),"instanceName":"1"});
            var Q4;
            Q4=makeQuery(id+"F9.opPattern","COPY",BODY,{"derivedFrom":makeQuery(id+"F6.opRevolve","SWEPT_BODY",BODY,{"disambiguationData":[OSD([sQuery(id+"F5.wireOp",EDGE,"E28"),sQuery(id+"F5.wireOp",EDGE,"E30")])]}),"instanceName":"2"});
            var Q5;
            Q5=makeQuery(id+"F9.opPattern","COPY",BODY,{"derivedFrom":makeQuery(id+"F7.opRevolve","SWEPT_BODY",BODY,{"disambiguationData":[OSD([sQuery(id+"F5.wireOp",EDGE,"E29"),sQuery(id+"F5.wireOp",EDGE,"E31")])]}),"instanceName":"2"});
            var Q6;
            Q6=makeQuery(id+"F9.opPattern","COPY",BODY,{"derivedFrom":makeQuery(id+"F6.opRevolve","SWEPT_BODY",BODY,{"disambiguationData":[OSD([sQuery(id+"F5.wireOp",EDGE,"E28"),sQuery(id+"F5.wireOp",EDGE,"E30")])]}),"instanceName":"3"});
            var Q7;
            Q7=makeQuery(id+"F9.opPattern","COPY",BODY,{"derivedFrom":makeQuery(id+"F7.opRevolve","SWEPT_BODY",BODY,{"disambiguationData":[OSD([sQuery(id+"F5.wireOp",EDGE,"E29"),sQuery(id+"F5.wireOp",EDGE,"E31")])]}),"instanceName":"3"});
            var Q8;
            Q8=makeQuery(id+"F9.opPattern","COPY",BODY,{"derivedFrom":makeQuery(id+"F6.opRevolve","SWEPT_BODY",BODY,{"disambiguationData":[OSD([sQuery(id+"F5.wireOp",EDGE,"E28"),sQuery(id+"F5.wireOp",EDGE,"E30")])]}),"instanceName":"4"});
            var Q9;
            Q9=makeQuery(id+"F9.opPattern","COPY",BODY,{"derivedFrom":makeQuery(id+"F7.opRevolve","SWEPT_BODY",BODY,{"disambiguationData":[OSD([sQuery(id+"F5.wireOp",EDGE,"E29"),sQuery(id+"F5.wireOp",EDGE,"E31")])]}),"instanceName":"4"});
            var Q10;
            Q10=makeQuery(id+"F9.opPattern","COPY",BODY,{"derivedFrom":makeQuery(id+"F6.opRevolve","SWEPT_BODY",BODY,{"disambiguationData":[OSD([sQuery(id+"F5.wireOp",EDGE,"E28"),sQuery(id+"F5.wireOp",EDGE,"E30")])]}),"instanceName":"5"});
            var Q11;
            Q11=makeQuery(id+"F9.opPattern","COPY",BODY,{"derivedFrom":makeQuery(id+"F7.opRevolve","SWEPT_BODY",BODY,{"disambiguationData":[OSD([sQuery(id+"F5.wireOp",EDGE,"E29"),sQuery(id+"F5.wireOp",EDGE,"E31")])]}),"instanceName":"5"});
            var Q12;
            Q12=makeQuery(id+"F9.opPattern","COPY",BODY,{"derivedFrom":makeQuery(id+"F6.opRevolve","SWEPT_BODY",BODY,{"disambiguationData":[OSD([sQuery(id+"F5.wireOp",EDGE,"E28"),sQuery(id+"F5.wireOp",EDGE,"E30")])]}),"instanceName":"6"});
            var Q13;
            Q13=makeQuery(id+"F9.opPattern","COPY",BODY,{"derivedFrom":makeQuery(id+"F7.opRevolve","SWEPT_BODY",BODY,{"disambiguationData":[OSD([sQuery(id+"F5.wireOp",EDGE,"E29"),sQuery(id+"F5.wireOp",EDGE,"E31")])]}),"instanceName":"6"});
            var Q14;
            Q14=makeQuery(id+"F9.opPattern","COPY",BODY,{"derivedFrom":makeQuery(id+"F6.opRevolve","SWEPT_BODY",BODY,{"disambiguationData":[OSD([sQuery(id+"F5.wireOp",EDGE,"E28"),sQuery(id+"F5.wireOp",EDGE,"E30")])]}),"instanceName":"7"});
            var Q15;
            Q15=makeQuery(id+"F9.opPattern","COPY",BODY,{"derivedFrom":makeQuery(id+"F7.opRevolve","SWEPT_BODY",BODY,{"disambiguationData":[OSD([sQuery(id+"F5.wireOp",EDGE,"E29"),sQuery(id+"F5.wireOp",EDGE,"E31")])]}),"instanceName":"7"});
            var Q16;
            Q16=makeQuery(id+"F9.opPattern","COPY",BODY,{"derivedFrom":makeQuery(id+"F6.opRevolve","SWEPT_BODY",BODY,{"disambiguationData":[OSD([sQuery(id+"F5.wireOp",EDGE,"E28"),sQuery(id+"F5.wireOp",EDGE,"E30")])]}),"instanceName":"8"});
            var Q17;
            Q17=makeQuery(id+"F9.opPattern","COPY",BODY,{"derivedFrom":makeQuery(id+"F7.opRevolve","SWEPT_BODY",BODY,{"disambiguationData":[OSD([sQuery(id+"F5.wireOp",EDGE,"E29"),sQuery(id+"F5.wireOp",EDGE,"E31")])]}),"instanceName":"8"});
            var Q18;
            Q18=makeQuery(id+"F9.opPattern","COPY",BODY,{"derivedFrom":makeQuery(id+"F6.opRevolve","SWEPT_BODY",BODY,{"disambiguationData":[OSD([sQuery(id+"F5.wireOp",EDGE,"E28"),sQuery(id+"F5.wireOp",EDGE,"E30")])]}),"instanceName":"9"});
            var Q19;
            Q19=makeQuery(id+"F9.opPattern","COPY",BODY,{"derivedFrom":makeQuery(id+"F7.opRevolve","SWEPT_BODY",BODY,{"disambiguationData":[OSD([sQuery(id+"F5.wireOp",EDGE,"E29"),sQuery(id+"F5.wireOp",EDGE,"E31")])]}),"instanceName":"9"});
            deleteBodies(context, id + "F11", {"entities" : qUnion([Q0, Q1, Q2, Q3, Q4, Q5, Q6, Q7, Q8, Q9, Q10, Q11, Q12, Q13, Q14, Q15, Q16, Q17, Q18, Q19])});
        }
    });
